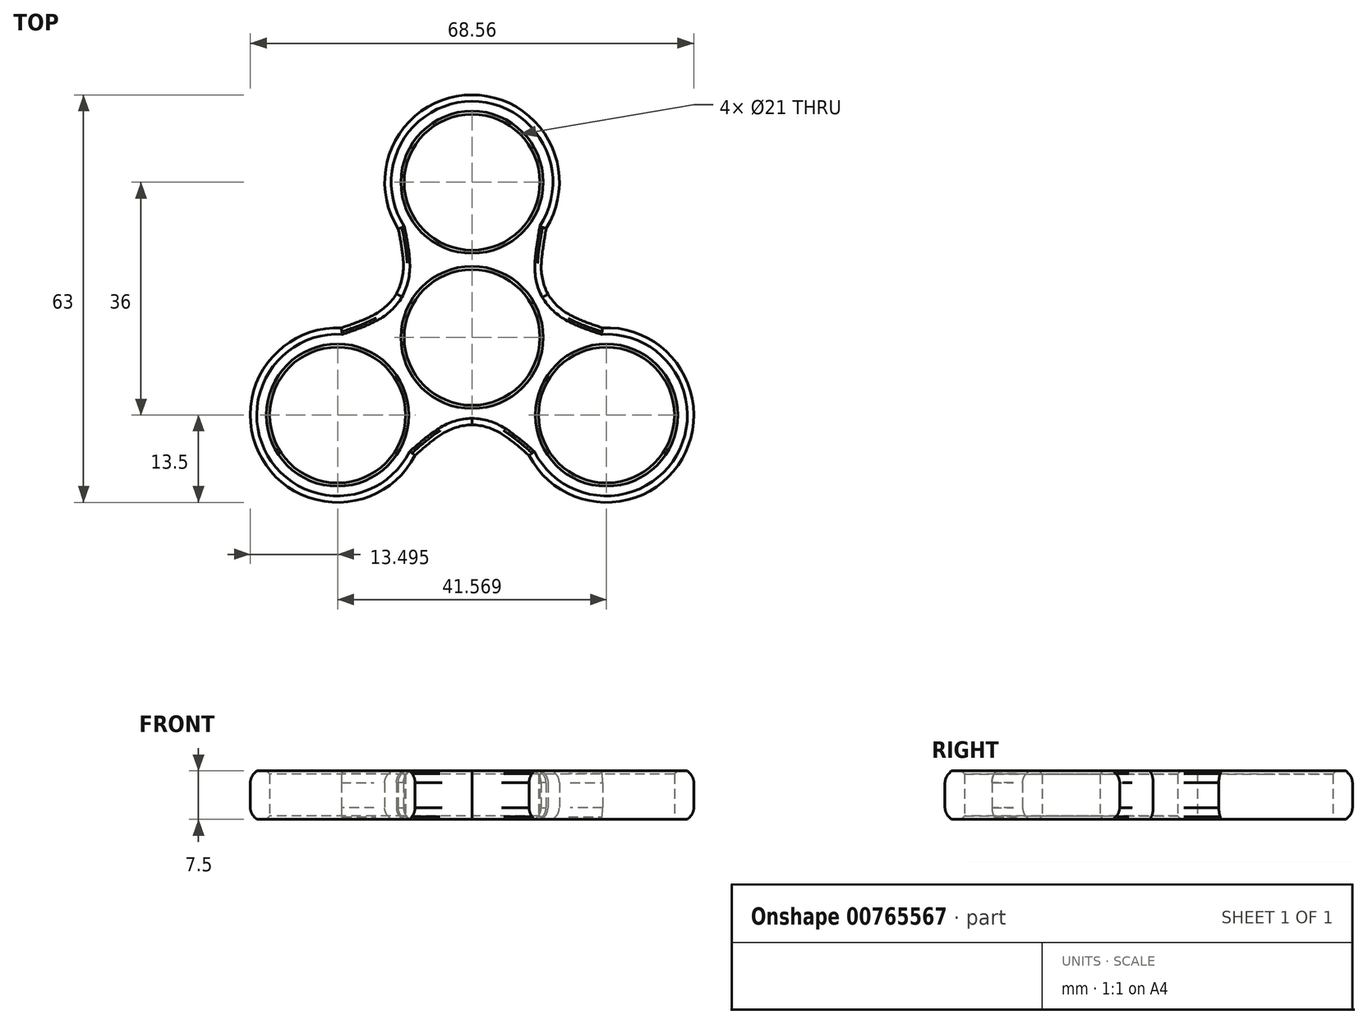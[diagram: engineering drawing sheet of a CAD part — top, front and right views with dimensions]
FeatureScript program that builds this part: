
annotation { "Feature Type Name" : "Feature", "Feature Type Description" : "" }
export const myFeature = defineFeature(function(context is Context, id is Id, definition is map)
    precondition{}
    {
        {
            var Q0;
            Q0=qCreatedBy(makeId("Top.planeOp"),FACE);
            var sketch = newSketch(context, id + "F0", { "sketchPlane" : qUnion([Q0])});
            skCircle(sketch, "E0", {"center": v(0, 0) * mm, "radius": 10.5 * mm});
            skSolve(sketch);
        }
        {
            var Q0;
            Q0=makeQuery(id+"F0.imprint","IMPRINT",FACE,{"disambiguationData":[TD([[makeQuery(id+"F0.imprint","IMPRINT",EDGE,{"derivedFrom":sQuery(id+"F0.wireOp",EDGE,"E0")}),1.0]])]});
            var sketch = newSketch(context, id + "F1", { "sketchPlane" : qUnion([Q0])});
            skCircle(sketch, "E1.0", {"center": v(0, 0) * mm, "radius": 13.5 * mm});
            skSolve(sketch);
        }
        {
            var Q0;
            Q0=qCreatedBy(makeId("Top.planeOp"),FACE);
            var sketch = newSketch(context, id + "F2", { "sketchPlane" : qUnion([Q0])});
            skCircle(sketch, "E2", {"center": v(0, 24) * mm, "radius": 10.5 * mm});
            skLineSegment(sketch, "E3", {"start": v(0, 0) * mm, "end": v(0, 24) * mm, "construction": true});
            skSolve(sketch);
        }
        {
            var Q0;
            Q0=qCreatedBy(makeId("Top.planeOp"),FACE);
            var sketch = newSketch(context, id + "F3", { "sketchPlane" : qUnion([Q0])});
            skLineSegment(sketch, "E4", {"start": v(0, 0) * mm, "end": v(20.78, -12) * mm, "construction": true});
            skPoint(sketch, "E5", {"position": v(20.78, -12) * mm});
            skCircle(sketch, "E6", {"center": v(20.78, -12) * mm, "radius": 10.5 * mm});
            skSolve(sketch);
        }
        {
            var Q0;
            Q0=qCreatedBy(makeId("Top.planeOp"),FACE);
            var sketch = newSketch(context, id + "F4", { "sketchPlane" : qUnion([Q0])});
            skLineSegment(sketch, "E7", {"start": v(0, 0) * mm, "end": v(-20.78, -12) * mm, "construction": true});
            skPoint(sketch, "E8", {"position": v(-20.78, -12) * mm});
            skCircle(sketch, "E9", {"center": v(-20.78, -12) * mm, "radius": 10.5 * mm});
            skSolve(sketch);
        }
        {
            var Q0;
            Q0=makeQuery(id+"F4.imprint","IMPRINT",FACE,{"disambiguationData":[TD([[makeQuery(id+"F4.imprint","IMPRINT",EDGE,{"derivedFrom":sQuery(id+"F4.wireOp",EDGE,"E9")}),1.0]])]});
            var sketch = newSketch(context, id + "F5", { "sketchPlane" : qUnion([Q0])});
            skCircle(sketch, "E10.0", {"center": v(-20.78, -12) * mm, "radius": 13.5 * mm});
            skCircle(sketch, "E11.0", {"center": v(20.78, -12) * mm, "radius": 13.5 * mm});
            skCircle(sketch, "E12.0", {"center": v(0, 24) * mm, "radius": 13.5 * mm});
            skSolve(sketch);
        }
        {
            var Q0;
            Q0=qCreatedBy(makeId("Top.planeOp"),FACE);
            var sketch = newSketch(context, id + "F6", { "sketchPlane" : qUnion([Q0])});
            skLineSegment(sketch, "E13", {"start": v(-20.78, -12) * mm, "end": v(-20.78, 1.3) * mm, "construction": true});
            skPoint(sketch, "E14", {"position": v(-20.78, 1.3) * mm});
            skSolve(sketch);
        }
        {
            var Q0;
            Q0=qCreatedBy(makeId("Top.planeOp"),FACE);
            var sketch = newSketch(context, id + "F7", { "sketchPlane" : qUnion([Q0])});
            skLineSegment(sketch, "E15", {"start": v(20.78, -12) * mm, "end": v(20.78, 1.3) * mm, "construction": true});
            skPoint(sketch, "E16", {"position": v(20.78, 1.3) * mm});
            skSolve(sketch);
        }
        {
            var Q0;
            Q0=qCreatedBy(makeId("Top.planeOp"),FACE);
            var sketch = newSketch(context, id + "F8", { "sketchPlane" : qUnion([Q0])});
            skLineSegment(sketch, "E17", {"start": v(20.78, -12) * mm, "end": v(9.27, -18.65) * mm, "construction": true});
            skPoint(sketch, "E18", {"position": v(9.27, -18.65) * mm});
            skSolve(sketch);
        }
        {
            var Q0;
            Q0=qCreatedBy(makeId("Top.planeOp"),FACE);
            var sketch = newSketch(context, id + "F9", { "sketchPlane" : qUnion([Q0])});
            skLineSegment(sketch, "E19", {"start": v(-20.78, -12) * mm, "end": v(-9.27, -18.65) * mm, "construction": true});
            skPoint(sketch, "E20", {"position": v(-9.27, -18.65) * mm});
            skSolve(sketch);
        }
        {
            var Q0;
            Q0=qCreatedBy(makeId("Top.planeOp"),FACE);
            var sketch = newSketch(context, id + "F10", { "sketchPlane" : qUnion([Q0])});
            skLineSegment(sketch, "E21", {"start": v(0, 24) * mm, "end": v(11.52, 17.35) * mm, "construction": true});
            skPoint(sketch, "E22", {"position": v(11.52, 17.35) * mm});
            skSolve(sketch);
        }
        {
            var Q0;
            Q0=qCreatedBy(makeId("Top.planeOp"),FACE);
            var sketch = newSketch(context, id + "F11", { "sketchPlane" : qUnion([Q0])});
            skLineSegment(sketch, "E23", {"start": v(0, 24) * mm, "end": v(-11.52, 17.35) * mm, "construction": true});
            skPoint(sketch, "E24", {"position": v(-11.52, 17.35) * mm});
            skSolve(sketch);
        }
        {
            var Q0;
            Q0=qCreatedBy(makeId("Top.planeOp"),FACE);
            var sketch = newSketch(context, id + "F12", { "sketchPlane" : qUnion([Q0])});
            skLineSegment(sketch, "E25", {"start": v(0, 0) * mm, "end": v(-11.52, 6.65) * mm, "construction": true});
            skPoint(sketch, "E26", {"position": v(-11.52, 6.65) * mm});
            skSolve(sketch);
        }
        {
            var Q0;
            Q0=qCreatedBy(makeId("Top.planeOp"),FACE);
            var sketch = newSketch(context, id + "F13", { "sketchPlane" : qUnion([Q0])});
            skLineSegment(sketch, "E27", {"start": v(0, 0) * mm, "end": v(11.52, 6.65) * mm, "construction": true});
            skPoint(sketch, "E28", {"position": v(11.52, 6.65) * mm});
            skSolve(sketch);
        }
        {
            var Q0;
            Q0=qCreatedBy(makeId("Top.planeOp"),FACE);
            var sketch = newSketch(context, id + "F14", { "sketchPlane" : qUnion([Q0])});
            skLineSegment(sketch, "E29", {"start": v(0, 0) * mm, "end": v(0, -13.3) * mm, "construction": true});
            skPoint(sketch, "E30", {"position": v(0, -13.3) * mm});
            skSolve(sketch);
        }
        {
            var Q0;
            Q0=qCreatedBy(makeId("Top.planeOp"),FACE);
            var sketch = newSketch(context, id + "F15", { "sketchPlane" : qUnion([Q0])});
            skFitSpline(sketch, "E31", {"points": [v(-20.78, 1.3) * mm, v(-11.52, 6.65) * mm, v(-11.52, 17.35) * mm], "startDerivative": vector(21.66, 7.06) * mm, "endDerivative": vector(-4.63, 23.05) * mm});
            skLineSegment(sketch, "E32", {"start": v(-20.78, 1.3) * mm, "end": v(-17.62, -0.3) * mm});
            skLineSegment(sketch, "E33", {"start": v(-17.62, -0.3) * mm, "end": v(-12.18, -1.05) * mm});
            skLineSegment(sketch, "E34", {"start": v(-12.18, -1.05) * mm, "end": v(-8.59, 9.21) * mm});
            skLineSegment(sketch, "E35", {"start": v(-8.59, 9.21) * mm, "end": v(-5.34, 11.64) * mm});
            skLineSegment(sketch, "E36", {"start": v(-5.34, 11.64) * mm, "end": v(-11.52, 17.35) * mm});
            skSolve(sketch);
        }
        {
            var Q0;
            Q0=qCreatedBy(makeId("Top.planeOp"),FACE);
            var sketch = newSketch(context, id + "F16", { "sketchPlane" : qUnion([Q0])});
            skFitSpline(sketch, "E37", {"points": [v(20.78, 1.3) * mm, v(11.52, 6.65) * mm, v(11.52, 17.35) * mm], "startDerivative": vector(-20.8, 6.31) * mm, "endDerivative": vector(3.23, 22.6) * mm});
            skLineSegment(sketch, "E38", {"start": v(11.52, 17.35) * mm, "end": v(5.33, 11.85) * mm});
            skLineSegment(sketch, "E39", {"start": v(5.33, 11.85) * mm, "end": v(13.1, -1.66) * mm});
            skLineSegment(sketch, "E40", {"start": v(13.1, -1.66) * mm, "end": v(20.78, 1.3) * mm});
            skSolve(sketch);
        }
        {
            var Q0;
            Q0=qCreatedBy(makeId("Top.planeOp"),FACE);
            var sketch = newSketch(context, id + "F17", { "sketchPlane" : qUnion([Q0])});
            skFitSpline(sketch, "E41", {"points": [v(-9.27, -18.65) * mm, v(0, -13.3) * mm, v(9.27, -18.65) * mm], "startDerivative": vector(16.43, 14.9) * mm, "endDerivative": vector(16.46, -14.71) * mm});
            skLineSegment(sketch, "E42", {"start": v(9.27, -18.65) * mm, "end": v(7.72, -10.63) * mm});
            skLineSegment(sketch, "E43", {"start": v(7.72, -10.63) * mm, "end": v(-7.8, -10.9) * mm});
            skLineSegment(sketch, "E44", {"start": v(-7.8, -10.9) * mm, "end": v(-9.27, -18.65) * mm});
            skSolve(sketch);
        }
        {
            var Q0;
            Q0=makeQuery(id+"F5.imprint","IMPRINT",FACE,{"disambiguationData":[TD([[makeQuery(id+"F5.imprint","IMPRINT",EDGE,{"derivedFrom":sQuery(id+"F5.wireOp",EDGE,"E11.0")}),1.0]])]});
            var Q1;
            Q1=makeQuery(id+"F5.imprint","IMPRINT",FACE,{"disambiguationData":[TD([[makeQuery(id+"F5.imprint","IMPRINT",EDGE,{"derivedFrom":sQuery(id+"F5.wireOp",EDGE,"E12.0")}),1.0]])]});
            var Q2;
            Q2=makeQuery(id+"F5.imprint","IMPRINT",FACE,{"disambiguationData":[TD([[makeQuery(id+"F5.imprint","IMPRINT",EDGE,{"derivedFrom":sQuery(id+"F5.wireOp",EDGE,"E10.0")}),1.0]])]});
            var Q3;
            Q3=makeQuery(id+"F1.imprint","IMPRINT",FACE,{"disambiguationData":[TD([[makeQuery(id+"F1.imprint","IMPRINT",EDGE,{"derivedFrom":sQuery(id+"F1.wireOp",EDGE,"E1.0")}),1.0]])]});
            var Q4;
            Q4=makeQuery(id+"F15.imprint","IMPRINT",FACE,{"disambiguationData":[TD([[makeQuery(id+"F15.imprint","IMPRINT",EDGE,{"derivedFrom":sQuery(id+"F15.wireOp",EDGE,"E31")}),-1.0]])]});
            var Q5;
            Q5=makeQuery(id+"F16.imprint","IMPRINT",FACE,{"disambiguationData":[TD([[makeQuery(id+"F16.imprint","IMPRINT",EDGE,{"derivedFrom":sQuery(id+"F16.wireOp",EDGE,"E37")}),1.0]])]});
            var Q6;
            Q6=makeQuery(id+"F17.imprint","IMPRINT",FACE,{"disambiguationData":[TD([[makeQuery(id+"F17.imprint","IMPRINT",EDGE,{"derivedFrom":sQuery(id+"F17.wireOp",EDGE,"E41")}),1.0]])]});
            extrude(context, id + "F18", {"entities" : qUnion([Q0, Q1, Q2, Q3, Q4, Q5, Q6]), "depth" : 7.5 * mm, "offsetDistance" : 25 * mm});
        }
        {
            var Q0;
            Q0=makeQuery(id+"F3.imprint","IMPRINT",FACE,{"disambiguationData":[TD([[makeQuery(id+"F3.imprint","IMPRINT",EDGE,{"derivedFrom":sQuery(id+"F3.wireOp",EDGE,"E6")}),1.0]])]});
            extrude(context, id + "F19", {"entities" : qUnion([Q0]), "operationType" : NewBodyOperationType.REMOVE, "depth" : 39.8 * mm, "offsetDistance" : 25 * mm});
        }
        {
            var Q0;
            Q0=makeQuery(id+"F2.imprint","IMPRINT",FACE,{"disambiguationData":[TD([[makeQuery(id+"F2.imprint","IMPRINT",EDGE,{"derivedFrom":sQuery(id+"F2.wireOp",EDGE,"E2")}),1.0]])]});
            extrude(context, id + "F20", {"entities" : qUnion([Q0]), "operationType" : NewBodyOperationType.REMOVE, "depth" : 25 * mm, "offsetDistance" : 25 * mm});
        }
        {
            var Q0;
            Q0=makeQuery(id+"F18.opExtrude","SWEPT_BODY",BODY,{"disambiguationData":[OSD([sQuery(id+"F4.wireOp",EDGE,"E9"),sQuery(id+"F5.wireOp",EDGE,"E10.0")])]});
            var Q1;
            Q1=makeQuery(id+"F18.opExtrude","SWEPT_BODY",BODY,{"disambiguationData":[OSD([sQuery(id+"F15.wireOp",EDGE,"E31"),sQuery(id+"F15.wireOp",EDGE,"E32"),sQuery(id+"F15.wireOp",EDGE,"E33"),sQuery(id+"F15.wireOp",EDGE,"E34"),sQuery(id+"F15.wireOp",EDGE,"E35"),sQuery(id+"F15.wireOp",EDGE,"E36")])]});
            var Q2;
            Q2=makeQuery(id+"F18.opExtrude","SWEPT_BODY",BODY,{"disambiguationData":[OSD([sQuery(id+"F0.wireOp",EDGE,"E0"),sQuery(id+"F1.wireOp",EDGE,"E1.0")])]});
            var Q3;
            Q3=makeQuery(id+"F18.opExtrude","SWEPT_BODY",BODY,{"disambiguationData":[OSD([sQuery(id+"F5.wireOp",EDGE,"E11.0")])]});
            var Q4;
            Q4=makeQuery(id+"F18.opExtrude","SWEPT_BODY",BODY,{"disambiguationData":[OSD([sQuery(id+"F17.wireOp",EDGE,"E41"),sQuery(id+"F17.wireOp",EDGE,"E42"),sQuery(id+"F17.wireOp",EDGE,"E43"),sQuery(id+"F17.wireOp",EDGE,"E44")])]});
            var Q5;
            Q5=makeQuery(id+"F18.opExtrude","SWEPT_BODY",BODY,{"disambiguationData":[OSD([sQuery(id+"F5.wireOp",EDGE,"E12.0")])]});
            var Q6;
            Q6=makeQuery(id+"F18.opExtrude","SWEPT_BODY",BODY,{"disambiguationData":[OSD([sQuery(id+"F16.wireOp",EDGE,"E37"),sQuery(id+"F16.wireOp",EDGE,"E38"),sQuery(id+"F16.wireOp",EDGE,"E39"),sQuery(id+"F16.wireOp",EDGE,"E40")])]});
            booleanBodies(context, id + "F21", {"operationType" : BooleanOperationType.UNION, "tools" : qUnion([Q0, Q1, Q2, Q3, Q4, Q5, Q6])});
        }
        {
            var Q0;
            Q0=makeQuery(id+"F21.opBoolean","INTERSECT",EDGE,{"disambiguationData":[OD(1.0)],"derivedFrom":[makeQuery(id+"F18.opExtrude","SWEPT_FACE",FACE,{"disambiguationData":[OSD([sQuery(id+"F1.wireOp",EDGE,"E1.0")])]}),makeQuery(id+"F18.opExtrude","SWEPT_FACE",FACE,{"disambiguationData":[OSD([sQuery(id+"F16.wireOp",EDGE,"E37")])]})]});
            var Q1;
            Q1=makeQuery(id+"F21.opBoolean","INTERSECT",EDGE,{"disambiguationData":[OD(0.0)],"derivedFrom":[makeQuery(id+"F18.opExtrude","SWEPT_FACE",FACE,{"disambiguationData":[OSD([sQuery(id+"F1.wireOp",EDGE,"E1.0")])]}),makeQuery(id+"F18.opExtrude","SWEPT_FACE",FACE,{"disambiguationData":[OSD([sQuery(id+"F16.wireOp",EDGE,"E37")])]})]});
            fillet(context, id + "F22", {"entities" : qUnion([Q0, Q1]), "radius" : 9 * mm, "tangentPropagation" : true, "allowEdgeOverflow" : false});
        }
        {
            var Q0;
            Q0=makeQuery(id+"F21.opBoolean","INTERSECT",EDGE,{"disambiguationData":[OD(0.0)],"derivedFrom":[makeQuery(id+"F18.opExtrude","SWEPT_FACE",FACE,{"disambiguationData":[OSD([sQuery(id+"F1.wireOp",EDGE,"E1.0")])]}),makeQuery(id+"F18.opExtrude","SWEPT_FACE",FACE,{"disambiguationData":[OSD([sQuery(id+"F17.wireOp",EDGE,"E41")])]})]});
            var Q1;
            Q1=makeQuery(id+"F21.opBoolean","INTERSECT",EDGE,{"disambiguationData":[OD(1.0)],"derivedFrom":[makeQuery(id+"F18.opExtrude","SWEPT_FACE",FACE,{"disambiguationData":[OSD([sQuery(id+"F1.wireOp",EDGE,"E1.0")])]}),makeQuery(id+"F18.opExtrude","SWEPT_FACE",FACE,{"disambiguationData":[OSD([sQuery(id+"F17.wireOp",EDGE,"E41")])]})]});
            fillet(context, id + "F23", {"entities" : qUnion([Q0, Q1]), "radius" : 9 * mm, "tangentPropagation" : true, "allowEdgeOverflow" : false});
        }
        {
            var Q0;
            Q0=makeQuery(id+"F21.opBoolean","INTERSECT",EDGE,{"disambiguationData":[OD(1.0)],"derivedFrom":[makeQuery(id+"F18.opExtrude","SWEPT_FACE",FACE,{"disambiguationData":[OSD([sQuery(id+"F1.wireOp",EDGE,"E1.0")])]}),makeQuery(id+"F18.opExtrude","SWEPT_FACE",FACE,{"disambiguationData":[OSD([sQuery(id+"F15.wireOp",EDGE,"E31")])]})]});
            var Q1;
            Q1=makeQuery(id+"F21.opBoolean","INTERSECT",EDGE,{"disambiguationData":[OD(0.0)],"derivedFrom":[makeQuery(id+"F18.opExtrude","SWEPT_FACE",FACE,{"disambiguationData":[OSD([sQuery(id+"F1.wireOp",EDGE,"E1.0")])]}),makeQuery(id+"F18.opExtrude","SWEPT_FACE",FACE,{"disambiguationData":[OSD([sQuery(id+"F15.wireOp",EDGE,"E31")])]})]});
            fillet(context, id + "F24", {"entities" : qUnion([Q0, Q1]), "radius" : 9 * mm, "tangentPropagation" : true, "allowEdgeOverflow" : false});
        }
        {
            var Q0;
            Q0=makeQuery(id+"F18.opExtrude","CAP_EDGE",EDGE,{"disambiguationData":[OSD([sQuery(id+"F0.wireOp",EDGE,"E0")])],"isStart":false});
            chamfer(context, id + "F25", {"entities" : qUnion([Q0]), "width" : 0.5 * mm, "tangentPropagation" : true});
        }
        {
            var Q0;
            Q0=makeQuery(id+"F19.boolean.opBoolean","INTERSECT",EDGE,{"derivedFrom":[makeQuery(id+"F18.opExtrude","CAP_FACE",FACE,{"disambiguationData":[OSD([sQuery(id+"F5.wireOp",EDGE,"E11.0")])],"isStart":false}),makeQuery(id+"F19.opExtrude","SWEPT_FACE",FACE,{"disambiguationData":[OSD([sQuery(id+"F3.wireOp",EDGE,"E6")])]})]});
            var Q1;
            Q1=makeQuery(id+"F18.opExtrude","CAP_EDGE",EDGE,{"disambiguationData":[OSD([sQuery(id+"F4.wireOp",EDGE,"E9")])],"isStart":false});
            var Q2;
            Q2=makeQuery(id+"F20.boolean.opBoolean","INTERSECT",EDGE,{"derivedFrom":[makeQuery(id+"F18.opExtrude","CAP_FACE",FACE,{"disambiguationData":[OSD([sQuery(id+"F5.wireOp",EDGE,"E12.0")])],"isStart":false}),makeQuery(id+"F20.opExtrude","SWEPT_FACE",FACE,{"disambiguationData":[OSD([sQuery(id+"F2.wireOp",EDGE,"E2")])]})]});
            chamfer(context, id + "F26", {"entities" : qUnion([Q0, Q1, Q2]), "width" : 0.5 * mm, "tangentPropagation" : true});
        }
        {
            var Q0;
            Q0=makeQuery(id+"F18.opExtrude","CAP_EDGE",EDGE,{"disambiguationData":[OSD([sQuery(id+"F5.wireOp",EDGE,"E11.0")])],"isStart":false});
            var Q1;
            {var subQ0=sQuery(id+"F5.wireOp",EDGE,"E11.0");var subQ2=sQuery(id+"F16.wireOp",EDGE,"E37");Q1=makeQuery(id+"F21.opBoolean","SPLIT",EDGE,{"disambiguationData":[TD([makeQuery(id+"F18.opExtrude","SWEPT_FACE",FACE,{"disambiguationData":[OSD([subQ0])]})])],"derivedFrom":makeQuery(id+"F18.opExtrude","CAP_EDGE",EDGE,{"disambiguationData":[OSD([subQ2])],"isStart":false})});}
            var Q2;
            {var subQ0=sQuery(id+"F16.wireOp",EDGE,"E37");var subQ1=sQuery(id+"F1.wireOp",EDGE,"E1.0");Q2=makeQuery(id+"F22.opFillet","BLEND_EDGE",EDGE,{"blendedFrom":[makeQuery(id+"F21.opBoolean","INTERSECT",EDGE,{"disambiguationData":[OD(0.0)],"derivedFrom":[makeQuery(id+"F18.opExtrude","SWEPT_FACE",FACE,{"disambiguationData":[OSD([subQ1])]}),makeQuery(id+"F18.opExtrude","SWEPT_FACE",FACE,{"disambiguationData":[OSD([subQ0])]})]}),makeQuery(id+"F21.opBoolean","MERGE",FACE,{"derivedFrom":[makeQuery(id+"F18.opExtrude","CAP_FACE",FACE,{"disambiguationData":[OSD([sQuery(id+"F0.wireOp",EDGE,"E0"),subQ1])],"isStart":false}),makeQuery(id+"F18.opExtrude","CAP_FACE",FACE,{"disambiguationData":[OSD([sQuery(id+"F4.wireOp",EDGE,"E9"),sQuery(id+"F5.wireOp",EDGE,"E10.0")])],"isStart":false}),makeQuery(id+"F18.opExtrude","CAP_FACE",FACE,{"disambiguationData":[OSD([sQuery(id+"F15.wireOp",EDGE,"E31"),sQuery(id+"F15.wireOp",EDGE,"E32"),sQuery(id+"F15.wireOp",EDGE,"E33"),sQuery(id+"F15.wireOp",EDGE,"E34"),sQuery(id+"F15.wireOp",EDGE,"E35"),sQuery(id+"F15.wireOp",EDGE,"E36")])],"isStart":false}),makeQuery(id+"F18.opExtrude","CAP_FACE",FACE,{"disambiguationData":[OSD([subQ0,sQuery(id+"F16.wireOp",EDGE,"E38"),sQuery(id+"F16.wireOp",EDGE,"E39"),sQuery(id+"F16.wireOp",EDGE,"E40")])],"isStart":false}),makeQuery(id+"F18.opExtrude","CAP_FACE",FACE,{"disambiguationData":[OSD([sQuery(id+"F17.wireOp",EDGE,"E41"),sQuery(id+"F17.wireOp",EDGE,"E42"),sQuery(id+"F17.wireOp",EDGE,"E43"),sQuery(id+"F17.wireOp",EDGE,"E44")])],"isStart":false}),makeQuery(id+"F18.opExtrude","CAP_FACE",FACE,{"disambiguationData":[OSD([sQuery(id+"F5.wireOp",EDGE,"E11.0")])],"isStart":false}),makeQuery(id+"F18.opExtrude","CAP_FACE",FACE,{"disambiguationData":[OSD([sQuery(id+"F5.wireOp",EDGE,"E12.0")])],"isStart":false})]})],"blendedInto":[makeQuery(id+"F21.opBoolean","MERGE",FACE,{"derivedFrom":[makeQuery(id+"F18.opExtrude","CAP_FACE",FACE,{"disambiguationData":[OSD([sQuery(id+"F0.wireOp",EDGE,"E0"),subQ1])],"isStart":false}),makeQuery(id+"F18.opExtrude","CAP_FACE",FACE,{"disambiguationData":[OSD([sQuery(id+"F4.wireOp",EDGE,"E9"),sQuery(id+"F5.wireOp",EDGE,"E10.0")])],"isStart":false}),makeQuery(id+"F18.opExtrude","CAP_FACE",FACE,{"disambiguationData":[OSD([sQuery(id+"F15.wireOp",EDGE,"E31"),sQuery(id+"F15.wireOp",EDGE,"E32"),sQuery(id+"F15.wireOp",EDGE,"E33"),sQuery(id+"F15.wireOp",EDGE,"E34"),sQuery(id+"F15.wireOp",EDGE,"E35"),sQuery(id+"F15.wireOp",EDGE,"E36")])],"isStart":false}),makeQuery(id+"F18.opExtrude","CAP_FACE",FACE,{"disambiguationData":[OSD([subQ0,sQuery(id+"F16.wireOp",EDGE,"E38"),sQuery(id+"F16.wireOp",EDGE,"E39"),sQuery(id+"F16.wireOp",EDGE,"E40")])],"isStart":false}),makeQuery(id+"F18.opExtrude","CAP_FACE",FACE,{"disambiguationData":[OSD([sQuery(id+"F17.wireOp",EDGE,"E41"),sQuery(id+"F17.wireOp",EDGE,"E42"),sQuery(id+"F17.wireOp",EDGE,"E43"),sQuery(id+"F17.wireOp",EDGE,"E44")])],"isStart":false}),makeQuery(id+"F18.opExtrude","CAP_FACE",FACE,{"disambiguationData":[OSD([sQuery(id+"F5.wireOp",EDGE,"E11.0")])],"isStart":false}),makeQuery(id+"F18.opExtrude","CAP_FACE",FACE,{"disambiguationData":[OSD([sQuery(id+"F5.wireOp",EDGE,"E12.0")])],"isStart":false})]})]});}
            var Q3;
            {var subQ0=sQuery(id+"F16.wireOp",EDGE,"E37");var subQ1=sQuery(id+"F1.wireOp",EDGE,"E1.0");Q3=makeQuery(id+"F22.opFillet","BLEND_EDGE",EDGE,{"blendedFrom":[makeQuery(id+"F21.opBoolean","INTERSECT",EDGE,{"disambiguationData":[OD(1.0)],"derivedFrom":[makeQuery(id+"F18.opExtrude","SWEPT_FACE",FACE,{"disambiguationData":[OSD([subQ1])]}),makeQuery(id+"F18.opExtrude","SWEPT_FACE",FACE,{"disambiguationData":[OSD([subQ0])]})]}),makeQuery(id+"F21.opBoolean","MERGE",FACE,{"derivedFrom":[makeQuery(id+"F18.opExtrude","CAP_FACE",FACE,{"disambiguationData":[OSD([sQuery(id+"F0.wireOp",EDGE,"E0"),subQ1])],"isStart":false}),makeQuery(id+"F18.opExtrude","CAP_FACE",FACE,{"disambiguationData":[OSD([sQuery(id+"F4.wireOp",EDGE,"E9"),sQuery(id+"F5.wireOp",EDGE,"E10.0")])],"isStart":false}),makeQuery(id+"F18.opExtrude","CAP_FACE",FACE,{"disambiguationData":[OSD([sQuery(id+"F15.wireOp",EDGE,"E31"),sQuery(id+"F15.wireOp",EDGE,"E32"),sQuery(id+"F15.wireOp",EDGE,"E33"),sQuery(id+"F15.wireOp",EDGE,"E34"),sQuery(id+"F15.wireOp",EDGE,"E35"),sQuery(id+"F15.wireOp",EDGE,"E36")])],"isStart":false}),makeQuery(id+"F18.opExtrude","CAP_FACE",FACE,{"disambiguationData":[OSD([subQ0,sQuery(id+"F16.wireOp",EDGE,"E38"),sQuery(id+"F16.wireOp",EDGE,"E39"),sQuery(id+"F16.wireOp",EDGE,"E40")])],"isStart":false}),makeQuery(id+"F18.opExtrude","CAP_FACE",FACE,{"disambiguationData":[OSD([sQuery(id+"F17.wireOp",EDGE,"E41"),sQuery(id+"F17.wireOp",EDGE,"E42"),sQuery(id+"F17.wireOp",EDGE,"E43"),sQuery(id+"F17.wireOp",EDGE,"E44")])],"isStart":false}),makeQuery(id+"F18.opExtrude","CAP_FACE",FACE,{"disambiguationData":[OSD([sQuery(id+"F5.wireOp",EDGE,"E11.0")])],"isStart":false}),makeQuery(id+"F18.opExtrude","CAP_FACE",FACE,{"disambiguationData":[OSD([sQuery(id+"F5.wireOp",EDGE,"E12.0")])],"isStart":false})]})],"blendedInto":[makeQuery(id+"F21.opBoolean","MERGE",FACE,{"derivedFrom":[makeQuery(id+"F18.opExtrude","CAP_FACE",FACE,{"disambiguationData":[OSD([sQuery(id+"F0.wireOp",EDGE,"E0"),subQ1])],"isStart":false}),makeQuery(id+"F18.opExtrude","CAP_FACE",FACE,{"disambiguationData":[OSD([sQuery(id+"F4.wireOp",EDGE,"E9"),sQuery(id+"F5.wireOp",EDGE,"E10.0")])],"isStart":false}),makeQuery(id+"F18.opExtrude","CAP_FACE",FACE,{"disambiguationData":[OSD([sQuery(id+"F15.wireOp",EDGE,"E31"),sQuery(id+"F15.wireOp",EDGE,"E32"),sQuery(id+"F15.wireOp",EDGE,"E33"),sQuery(id+"F15.wireOp",EDGE,"E34"),sQuery(id+"F15.wireOp",EDGE,"E35"),sQuery(id+"F15.wireOp",EDGE,"E36")])],"isStart":false}),makeQuery(id+"F18.opExtrude","CAP_FACE",FACE,{"disambiguationData":[OSD([subQ0,sQuery(id+"F16.wireOp",EDGE,"E38"),sQuery(id+"F16.wireOp",EDGE,"E39"),sQuery(id+"F16.wireOp",EDGE,"E40")])],"isStart":false}),makeQuery(id+"F18.opExtrude","CAP_FACE",FACE,{"disambiguationData":[OSD([sQuery(id+"F17.wireOp",EDGE,"E41"),sQuery(id+"F17.wireOp",EDGE,"E42"),sQuery(id+"F17.wireOp",EDGE,"E43"),sQuery(id+"F17.wireOp",EDGE,"E44")])],"isStart":false}),makeQuery(id+"F18.opExtrude","CAP_FACE",FACE,{"disambiguationData":[OSD([sQuery(id+"F5.wireOp",EDGE,"E11.0")])],"isStart":false}),makeQuery(id+"F18.opExtrude","CAP_FACE",FACE,{"disambiguationData":[OSD([sQuery(id+"F5.wireOp",EDGE,"E12.0")])],"isStart":false})]})]});}
            var Q4;
            {var subQ1=sQuery(id+"F16.wireOp",EDGE,"E37");var subQ2=sQuery(id+"F5.wireOp",EDGE,"E12.0");Q4=makeQuery(id+"F21.opBoolean","SPLIT",EDGE,{"disambiguationData":[TD([makeQuery(id+"F18.opExtrude","SWEPT_FACE",FACE,{"disambiguationData":[OSD([subQ2])]})])],"derivedFrom":makeQuery(id+"F18.opExtrude","CAP_EDGE",EDGE,{"disambiguationData":[OSD([subQ1])],"isStart":false})});}
            var Q5;
            Q5=makeQuery(id+"F18.opExtrude","CAP_EDGE",EDGE,{"disambiguationData":[OSD([sQuery(id+"F5.wireOp",EDGE,"E12.0")])],"isStart":false});
            var Q6;
            {var subQ1=sQuery(id+"F5.wireOp",EDGE,"E12.0");var subQ2=sQuery(id+"F15.wireOp",EDGE,"E31");Q6=makeQuery(id+"F21.opBoolean","SPLIT",EDGE,{"disambiguationData":[TD([makeQuery(id+"F18.opExtrude","SWEPT_FACE",FACE,{"disambiguationData":[OSD([subQ1])]})])],"derivedFrom":makeQuery(id+"F18.opExtrude","CAP_EDGE",EDGE,{"disambiguationData":[OSD([subQ2])],"isStart":false})});}
            var Q7;
            {var subQ0=sQuery(id+"F15.wireOp",EDGE,"E31");var subQ1=sQuery(id+"F1.wireOp",EDGE,"E1.0");Q7=makeQuery(id+"F24.opFillet","BLEND_EDGE",EDGE,{"blendedFrom":[makeQuery(id+"F21.opBoolean","INTERSECT",EDGE,{"disambiguationData":[OD(1.0)],"derivedFrom":[makeQuery(id+"F18.opExtrude","SWEPT_FACE",FACE,{"disambiguationData":[OSD([subQ1])]}),makeQuery(id+"F18.opExtrude","SWEPT_FACE",FACE,{"disambiguationData":[OSD([subQ0])]})]}),makeQuery(id+"F21.opBoolean","MERGE",FACE,{"derivedFrom":[makeQuery(id+"F18.opExtrude","CAP_FACE",FACE,{"disambiguationData":[OSD([sQuery(id+"F0.wireOp",EDGE,"E0"),subQ1])],"isStart":false}),makeQuery(id+"F18.opExtrude","CAP_FACE",FACE,{"disambiguationData":[OSD([sQuery(id+"F4.wireOp",EDGE,"E9"),sQuery(id+"F5.wireOp",EDGE,"E10.0")])],"isStart":false}),makeQuery(id+"F18.opExtrude","CAP_FACE",FACE,{"disambiguationData":[OSD([subQ0,sQuery(id+"F15.wireOp",EDGE,"E32"),sQuery(id+"F15.wireOp",EDGE,"E33"),sQuery(id+"F15.wireOp",EDGE,"E34"),sQuery(id+"F15.wireOp",EDGE,"E35"),sQuery(id+"F15.wireOp",EDGE,"E36")])],"isStart":false}),makeQuery(id+"F18.opExtrude","CAP_FACE",FACE,{"disambiguationData":[OSD([sQuery(id+"F16.wireOp",EDGE,"E37"),sQuery(id+"F16.wireOp",EDGE,"E38"),sQuery(id+"F16.wireOp",EDGE,"E39"),sQuery(id+"F16.wireOp",EDGE,"E40")])],"isStart":false}),makeQuery(id+"F18.opExtrude","CAP_FACE",FACE,{"disambiguationData":[OSD([sQuery(id+"F17.wireOp",EDGE,"E41"),sQuery(id+"F17.wireOp",EDGE,"E42"),sQuery(id+"F17.wireOp",EDGE,"E43"),sQuery(id+"F17.wireOp",EDGE,"E44")])],"isStart":false}),makeQuery(id+"F18.opExtrude","CAP_FACE",FACE,{"disambiguationData":[OSD([sQuery(id+"F5.wireOp",EDGE,"E11.0")])],"isStart":false}),makeQuery(id+"F18.opExtrude","CAP_FACE",FACE,{"disambiguationData":[OSD([sQuery(id+"F5.wireOp",EDGE,"E12.0")])],"isStart":false})]})],"blendedInto":[makeQuery(id+"F21.opBoolean","MERGE",FACE,{"derivedFrom":[makeQuery(id+"F18.opExtrude","CAP_FACE",FACE,{"disambiguationData":[OSD([sQuery(id+"F0.wireOp",EDGE,"E0"),subQ1])],"isStart":false}),makeQuery(id+"F18.opExtrude","CAP_FACE",FACE,{"disambiguationData":[OSD([sQuery(id+"F4.wireOp",EDGE,"E9"),sQuery(id+"F5.wireOp",EDGE,"E10.0")])],"isStart":false}),makeQuery(id+"F18.opExtrude","CAP_FACE",FACE,{"disambiguationData":[OSD([subQ0,sQuery(id+"F15.wireOp",EDGE,"E32"),sQuery(id+"F15.wireOp",EDGE,"E33"),sQuery(id+"F15.wireOp",EDGE,"E34"),sQuery(id+"F15.wireOp",EDGE,"E35"),sQuery(id+"F15.wireOp",EDGE,"E36")])],"isStart":false}),makeQuery(id+"F18.opExtrude","CAP_FACE",FACE,{"disambiguationData":[OSD([sQuery(id+"F16.wireOp",EDGE,"E37"),sQuery(id+"F16.wireOp",EDGE,"E38"),sQuery(id+"F16.wireOp",EDGE,"E39"),sQuery(id+"F16.wireOp",EDGE,"E40")])],"isStart":false}),makeQuery(id+"F18.opExtrude","CAP_FACE",FACE,{"disambiguationData":[OSD([sQuery(id+"F17.wireOp",EDGE,"E41"),sQuery(id+"F17.wireOp",EDGE,"E42"),sQuery(id+"F17.wireOp",EDGE,"E43"),sQuery(id+"F17.wireOp",EDGE,"E44")])],"isStart":false}),makeQuery(id+"F18.opExtrude","CAP_FACE",FACE,{"disambiguationData":[OSD([sQuery(id+"F5.wireOp",EDGE,"E11.0")])],"isStart":false}),makeQuery(id+"F18.opExtrude","CAP_FACE",FACE,{"disambiguationData":[OSD([sQuery(id+"F5.wireOp",EDGE,"E12.0")])],"isStart":false})]})]});}
            var Q8;
            {var subQ0=sQuery(id+"F15.wireOp",EDGE,"E31");var subQ1=sQuery(id+"F1.wireOp",EDGE,"E1.0");Q8=makeQuery(id+"F24.opFillet","BLEND_EDGE",EDGE,{"blendedFrom":[makeQuery(id+"F21.opBoolean","INTERSECT",EDGE,{"disambiguationData":[OD(0.0)],"derivedFrom":[makeQuery(id+"F18.opExtrude","SWEPT_FACE",FACE,{"disambiguationData":[OSD([subQ1])]}),makeQuery(id+"F18.opExtrude","SWEPT_FACE",FACE,{"disambiguationData":[OSD([subQ0])]})]}),makeQuery(id+"F21.opBoolean","MERGE",FACE,{"derivedFrom":[makeQuery(id+"F18.opExtrude","CAP_FACE",FACE,{"disambiguationData":[OSD([sQuery(id+"F0.wireOp",EDGE,"E0"),subQ1])],"isStart":false}),makeQuery(id+"F18.opExtrude","CAP_FACE",FACE,{"disambiguationData":[OSD([sQuery(id+"F4.wireOp",EDGE,"E9"),sQuery(id+"F5.wireOp",EDGE,"E10.0")])],"isStart":false}),makeQuery(id+"F18.opExtrude","CAP_FACE",FACE,{"disambiguationData":[OSD([subQ0,sQuery(id+"F15.wireOp",EDGE,"E32"),sQuery(id+"F15.wireOp",EDGE,"E33"),sQuery(id+"F15.wireOp",EDGE,"E34"),sQuery(id+"F15.wireOp",EDGE,"E35"),sQuery(id+"F15.wireOp",EDGE,"E36")])],"isStart":false}),makeQuery(id+"F18.opExtrude","CAP_FACE",FACE,{"disambiguationData":[OSD([sQuery(id+"F16.wireOp",EDGE,"E37"),sQuery(id+"F16.wireOp",EDGE,"E38"),sQuery(id+"F16.wireOp",EDGE,"E39"),sQuery(id+"F16.wireOp",EDGE,"E40")])],"isStart":false}),makeQuery(id+"F18.opExtrude","CAP_FACE",FACE,{"disambiguationData":[OSD([sQuery(id+"F17.wireOp",EDGE,"E41"),sQuery(id+"F17.wireOp",EDGE,"E42"),sQuery(id+"F17.wireOp",EDGE,"E43"),sQuery(id+"F17.wireOp",EDGE,"E44")])],"isStart":false}),makeQuery(id+"F18.opExtrude","CAP_FACE",FACE,{"disambiguationData":[OSD([sQuery(id+"F5.wireOp",EDGE,"E11.0")])],"isStart":false}),makeQuery(id+"F18.opExtrude","CAP_FACE",FACE,{"disambiguationData":[OSD([sQuery(id+"F5.wireOp",EDGE,"E12.0")])],"isStart":false})]})],"blendedInto":[makeQuery(id+"F21.opBoolean","MERGE",FACE,{"derivedFrom":[makeQuery(id+"F18.opExtrude","CAP_FACE",FACE,{"disambiguationData":[OSD([sQuery(id+"F0.wireOp",EDGE,"E0"),subQ1])],"isStart":false}),makeQuery(id+"F18.opExtrude","CAP_FACE",FACE,{"disambiguationData":[OSD([sQuery(id+"F4.wireOp",EDGE,"E9"),sQuery(id+"F5.wireOp",EDGE,"E10.0")])],"isStart":false}),makeQuery(id+"F18.opExtrude","CAP_FACE",FACE,{"disambiguationData":[OSD([subQ0,sQuery(id+"F15.wireOp",EDGE,"E32"),sQuery(id+"F15.wireOp",EDGE,"E33"),sQuery(id+"F15.wireOp",EDGE,"E34"),sQuery(id+"F15.wireOp",EDGE,"E35"),sQuery(id+"F15.wireOp",EDGE,"E36")])],"isStart":false}),makeQuery(id+"F18.opExtrude","CAP_FACE",FACE,{"disambiguationData":[OSD([sQuery(id+"F16.wireOp",EDGE,"E37"),sQuery(id+"F16.wireOp",EDGE,"E38"),sQuery(id+"F16.wireOp",EDGE,"E39"),sQuery(id+"F16.wireOp",EDGE,"E40")])],"isStart":false}),makeQuery(id+"F18.opExtrude","CAP_FACE",FACE,{"disambiguationData":[OSD([sQuery(id+"F17.wireOp",EDGE,"E41"),sQuery(id+"F17.wireOp",EDGE,"E42"),sQuery(id+"F17.wireOp",EDGE,"E43"),sQuery(id+"F17.wireOp",EDGE,"E44")])],"isStart":false}),makeQuery(id+"F18.opExtrude","CAP_FACE",FACE,{"disambiguationData":[OSD([sQuery(id+"F5.wireOp",EDGE,"E11.0")])],"isStart":false}),makeQuery(id+"F18.opExtrude","CAP_FACE",FACE,{"disambiguationData":[OSD([sQuery(id+"F5.wireOp",EDGE,"E12.0")])],"isStart":false})]})]});}
            var Q9;
            {var subQ0=sQuery(id+"F5.wireOp",EDGE,"E10.0");var subQ2=sQuery(id+"F15.wireOp",EDGE,"E31");Q9=makeQuery(id+"F21.opBoolean","SPLIT",EDGE,{"disambiguationData":[TD([makeQuery(id+"F18.opExtrude","SWEPT_FACE",FACE,{"disambiguationData":[OSD([subQ0])]})])],"derivedFrom":makeQuery(id+"F18.opExtrude","CAP_EDGE",EDGE,{"disambiguationData":[OSD([subQ2])],"isStart":false})});}
            var Q10;
            Q10=makeQuery(id+"F18.opExtrude","CAP_EDGE",EDGE,{"disambiguationData":[OSD([sQuery(id+"F5.wireOp",EDGE,"E10.0")])],"isStart":false});
            var Q11;
            {var subQ0=sQuery(id+"F5.wireOp",EDGE,"E10.0");var subQ1=sQuery(id+"F17.wireOp",EDGE,"E41");Q11=makeQuery(id+"F21.opBoolean","SPLIT",EDGE,{"disambiguationData":[TD([makeQuery(id+"F18.opExtrude","SWEPT_FACE",FACE,{"disambiguationData":[OSD([subQ0])]})])],"derivedFrom":makeQuery(id+"F18.opExtrude","CAP_EDGE",EDGE,{"disambiguationData":[OSD([subQ1])],"isStart":false})});}
            var Q12;
            {var subQ0=sQuery(id+"F17.wireOp",EDGE,"E41");var subQ1=sQuery(id+"F1.wireOp",EDGE,"E1.0");Q12=makeQuery(id+"F23.opFillet","BLEND_EDGE",EDGE,{"blendedFrom":[makeQuery(id+"F21.opBoolean","INTERSECT",EDGE,{"disambiguationData":[OD(0.0)],"derivedFrom":[makeQuery(id+"F18.opExtrude","SWEPT_FACE",FACE,{"disambiguationData":[OSD([subQ1])]}),makeQuery(id+"F18.opExtrude","SWEPT_FACE",FACE,{"disambiguationData":[OSD([subQ0])]})]}),makeQuery(id+"F21.opBoolean","MERGE",FACE,{"derivedFrom":[makeQuery(id+"F18.opExtrude","CAP_FACE",FACE,{"disambiguationData":[OSD([sQuery(id+"F0.wireOp",EDGE,"E0"),subQ1])],"isStart":false}),makeQuery(id+"F18.opExtrude","CAP_FACE",FACE,{"disambiguationData":[OSD([sQuery(id+"F4.wireOp",EDGE,"E9"),sQuery(id+"F5.wireOp",EDGE,"E10.0")])],"isStart":false}),makeQuery(id+"F18.opExtrude","CAP_FACE",FACE,{"disambiguationData":[OSD([sQuery(id+"F15.wireOp",EDGE,"E31"),sQuery(id+"F15.wireOp",EDGE,"E32"),sQuery(id+"F15.wireOp",EDGE,"E33"),sQuery(id+"F15.wireOp",EDGE,"E34"),sQuery(id+"F15.wireOp",EDGE,"E35"),sQuery(id+"F15.wireOp",EDGE,"E36")])],"isStart":false}),makeQuery(id+"F18.opExtrude","CAP_FACE",FACE,{"disambiguationData":[OSD([sQuery(id+"F16.wireOp",EDGE,"E37"),sQuery(id+"F16.wireOp",EDGE,"E38"),sQuery(id+"F16.wireOp",EDGE,"E39"),sQuery(id+"F16.wireOp",EDGE,"E40")])],"isStart":false}),makeQuery(id+"F18.opExtrude","CAP_FACE",FACE,{"disambiguationData":[OSD([subQ0,sQuery(id+"F17.wireOp",EDGE,"E42"),sQuery(id+"F17.wireOp",EDGE,"E43"),sQuery(id+"F17.wireOp",EDGE,"E44")])],"isStart":false}),makeQuery(id+"F18.opExtrude","CAP_FACE",FACE,{"disambiguationData":[OSD([sQuery(id+"F5.wireOp",EDGE,"E11.0")])],"isStart":false}),makeQuery(id+"F18.opExtrude","CAP_FACE",FACE,{"disambiguationData":[OSD([sQuery(id+"F5.wireOp",EDGE,"E12.0")])],"isStart":false})]})],"blendedInto":[makeQuery(id+"F21.opBoolean","MERGE",FACE,{"derivedFrom":[makeQuery(id+"F18.opExtrude","CAP_FACE",FACE,{"disambiguationData":[OSD([sQuery(id+"F0.wireOp",EDGE,"E0"),subQ1])],"isStart":false}),makeQuery(id+"F18.opExtrude","CAP_FACE",FACE,{"disambiguationData":[OSD([sQuery(id+"F4.wireOp",EDGE,"E9"),sQuery(id+"F5.wireOp",EDGE,"E10.0")])],"isStart":false}),makeQuery(id+"F18.opExtrude","CAP_FACE",FACE,{"disambiguationData":[OSD([sQuery(id+"F15.wireOp",EDGE,"E31"),sQuery(id+"F15.wireOp",EDGE,"E32"),sQuery(id+"F15.wireOp",EDGE,"E33"),sQuery(id+"F15.wireOp",EDGE,"E34"),sQuery(id+"F15.wireOp",EDGE,"E35"),sQuery(id+"F15.wireOp",EDGE,"E36")])],"isStart":false}),makeQuery(id+"F18.opExtrude","CAP_FACE",FACE,{"disambiguationData":[OSD([sQuery(id+"F16.wireOp",EDGE,"E37"),sQuery(id+"F16.wireOp",EDGE,"E38"),sQuery(id+"F16.wireOp",EDGE,"E39"),sQuery(id+"F16.wireOp",EDGE,"E40")])],"isStart":false}),makeQuery(id+"F18.opExtrude","CAP_FACE",FACE,{"disambiguationData":[OSD([subQ0,sQuery(id+"F17.wireOp",EDGE,"E42"),sQuery(id+"F17.wireOp",EDGE,"E43"),sQuery(id+"F17.wireOp",EDGE,"E44")])],"isStart":false}),makeQuery(id+"F18.opExtrude","CAP_FACE",FACE,{"disambiguationData":[OSD([sQuery(id+"F5.wireOp",EDGE,"E11.0")])],"isStart":false}),makeQuery(id+"F18.opExtrude","CAP_FACE",FACE,{"disambiguationData":[OSD([sQuery(id+"F5.wireOp",EDGE,"E12.0")])],"isStart":false})]})]});}
            var Q13;
            {var subQ0=sQuery(id+"F17.wireOp",EDGE,"E41");var subQ1=sQuery(id+"F1.wireOp",EDGE,"E1.0");Q13=makeQuery(id+"F23.opFillet","BLEND_EDGE",EDGE,{"blendedFrom":[makeQuery(id+"F21.opBoolean","INTERSECT",EDGE,{"disambiguationData":[OD(1.0)],"derivedFrom":[makeQuery(id+"F18.opExtrude","SWEPT_FACE",FACE,{"disambiguationData":[OSD([subQ1])]}),makeQuery(id+"F18.opExtrude","SWEPT_FACE",FACE,{"disambiguationData":[OSD([subQ0])]})]}),makeQuery(id+"F21.opBoolean","MERGE",FACE,{"derivedFrom":[makeQuery(id+"F18.opExtrude","CAP_FACE",FACE,{"disambiguationData":[OSD([sQuery(id+"F0.wireOp",EDGE,"E0"),subQ1])],"isStart":false}),makeQuery(id+"F18.opExtrude","CAP_FACE",FACE,{"disambiguationData":[OSD([sQuery(id+"F4.wireOp",EDGE,"E9"),sQuery(id+"F5.wireOp",EDGE,"E10.0")])],"isStart":false}),makeQuery(id+"F18.opExtrude","CAP_FACE",FACE,{"disambiguationData":[OSD([sQuery(id+"F15.wireOp",EDGE,"E31"),sQuery(id+"F15.wireOp",EDGE,"E32"),sQuery(id+"F15.wireOp",EDGE,"E33"),sQuery(id+"F15.wireOp",EDGE,"E34"),sQuery(id+"F15.wireOp",EDGE,"E35"),sQuery(id+"F15.wireOp",EDGE,"E36")])],"isStart":false}),makeQuery(id+"F18.opExtrude","CAP_FACE",FACE,{"disambiguationData":[OSD([sQuery(id+"F16.wireOp",EDGE,"E37"),sQuery(id+"F16.wireOp",EDGE,"E38"),sQuery(id+"F16.wireOp",EDGE,"E39"),sQuery(id+"F16.wireOp",EDGE,"E40")])],"isStart":false}),makeQuery(id+"F18.opExtrude","CAP_FACE",FACE,{"disambiguationData":[OSD([subQ0,sQuery(id+"F17.wireOp",EDGE,"E42"),sQuery(id+"F17.wireOp",EDGE,"E43"),sQuery(id+"F17.wireOp",EDGE,"E44")])],"isStart":false}),makeQuery(id+"F18.opExtrude","CAP_FACE",FACE,{"disambiguationData":[OSD([sQuery(id+"F5.wireOp",EDGE,"E11.0")])],"isStart":false}),makeQuery(id+"F18.opExtrude","CAP_FACE",FACE,{"disambiguationData":[OSD([sQuery(id+"F5.wireOp",EDGE,"E12.0")])],"isStart":false})]})],"blendedInto":[makeQuery(id+"F21.opBoolean","MERGE",FACE,{"derivedFrom":[makeQuery(id+"F18.opExtrude","CAP_FACE",FACE,{"disambiguationData":[OSD([sQuery(id+"F0.wireOp",EDGE,"E0"),subQ1])],"isStart":false}),makeQuery(id+"F18.opExtrude","CAP_FACE",FACE,{"disambiguationData":[OSD([sQuery(id+"F4.wireOp",EDGE,"E9"),sQuery(id+"F5.wireOp",EDGE,"E10.0")])],"isStart":false}),makeQuery(id+"F18.opExtrude","CAP_FACE",FACE,{"disambiguationData":[OSD([sQuery(id+"F15.wireOp",EDGE,"E31"),sQuery(id+"F15.wireOp",EDGE,"E32"),sQuery(id+"F15.wireOp",EDGE,"E33"),sQuery(id+"F15.wireOp",EDGE,"E34"),sQuery(id+"F15.wireOp",EDGE,"E35"),sQuery(id+"F15.wireOp",EDGE,"E36")])],"isStart":false}),makeQuery(id+"F18.opExtrude","CAP_FACE",FACE,{"disambiguationData":[OSD([sQuery(id+"F16.wireOp",EDGE,"E37"),sQuery(id+"F16.wireOp",EDGE,"E38"),sQuery(id+"F16.wireOp",EDGE,"E39"),sQuery(id+"F16.wireOp",EDGE,"E40")])],"isStart":false}),makeQuery(id+"F18.opExtrude","CAP_FACE",FACE,{"disambiguationData":[OSD([subQ0,sQuery(id+"F17.wireOp",EDGE,"E42"),sQuery(id+"F17.wireOp",EDGE,"E43"),sQuery(id+"F17.wireOp",EDGE,"E44")])],"isStart":false}),makeQuery(id+"F18.opExtrude","CAP_FACE",FACE,{"disambiguationData":[OSD([sQuery(id+"F5.wireOp",EDGE,"E11.0")])],"isStart":false}),makeQuery(id+"F18.opExtrude","CAP_FACE",FACE,{"disambiguationData":[OSD([sQuery(id+"F5.wireOp",EDGE,"E12.0")])],"isStart":false})]})]});}
            var Q14;
            {var subQ0=sQuery(id+"F17.wireOp",EDGE,"E41");var subQ1=sQuery(id+"F5.wireOp",EDGE,"E11.0");Q14=makeQuery(id+"F21.opBoolean","SPLIT",EDGE,{"disambiguationData":[TD([makeQuery(id+"F18.opExtrude","SWEPT_FACE",FACE,{"disambiguationData":[OSD([subQ1])]})])],"derivedFrom":makeQuery(id+"F18.opExtrude","CAP_EDGE",EDGE,{"disambiguationData":[OSD([subQ0])],"isStart":false})});}
            chamfer(context, id + "F27", {"entities" : qUnion([Q0, Q1, Q2, Q3, Q4, Q5, Q6, Q7, Q8, Q9, Q10, Q11, Q12, Q13, Q14]), "width" : 1 * mm, "tangentPropagation" : true});
        }
        {
            var Q0;
            Q0=makeQuery(id+"F18.opExtrude","CAP_EDGE",EDGE,{"disambiguationData":[OSD([sQuery(id+"F5.wireOp",EDGE,"E11.0")])],"isStart":true});
            var Q1;
            {var subQ0=sQuery(id+"F5.wireOp",EDGE,"E11.0");var subQ2=sQuery(id+"F16.wireOp",EDGE,"E37");Q1=makeQuery(id+"F21.opBoolean","SPLIT",EDGE,{"disambiguationData":[TD([makeQuery(id+"F18.opExtrude","SWEPT_FACE",FACE,{"disambiguationData":[OSD([subQ0])]})])],"derivedFrom":makeQuery(id+"F18.opExtrude","CAP_EDGE",EDGE,{"disambiguationData":[OSD([subQ2])],"isStart":true})});}
            var Q2;
            {var subQ0=sQuery(id+"F16.wireOp",EDGE,"E37");var subQ1=sQuery(id+"F1.wireOp",EDGE,"E1.0");Q2=makeQuery(id+"F22.opFillet","BLEND_EDGE",EDGE,{"blendedFrom":[makeQuery(id+"F21.opBoolean","INTERSECT",EDGE,{"disambiguationData":[OD(0.0)],"derivedFrom":[makeQuery(id+"F18.opExtrude","SWEPT_FACE",FACE,{"disambiguationData":[OSD([subQ1])]}),makeQuery(id+"F18.opExtrude","SWEPT_FACE",FACE,{"disambiguationData":[OSD([subQ0])]})]}),makeQuery(id+"F21.opBoolean","MERGE",FACE,{"derivedFrom":[makeQuery(id+"F18.opExtrude","CAP_FACE",FACE,{"disambiguationData":[OSD([sQuery(id+"F0.wireOp",EDGE,"E0"),subQ1])],"isStart":true}),makeQuery(id+"F18.opExtrude","CAP_FACE",FACE,{"disambiguationData":[OSD([sQuery(id+"F4.wireOp",EDGE,"E9"),sQuery(id+"F5.wireOp",EDGE,"E10.0")])],"isStart":true}),makeQuery(id+"F18.opExtrude","CAP_FACE",FACE,{"disambiguationData":[OSD([sQuery(id+"F15.wireOp",EDGE,"E31"),sQuery(id+"F15.wireOp",EDGE,"E32"),sQuery(id+"F15.wireOp",EDGE,"E33"),sQuery(id+"F15.wireOp",EDGE,"E34"),sQuery(id+"F15.wireOp",EDGE,"E35"),sQuery(id+"F15.wireOp",EDGE,"E36")])],"isStart":true}),makeQuery(id+"F18.opExtrude","CAP_FACE",FACE,{"disambiguationData":[OSD([subQ0,sQuery(id+"F16.wireOp",EDGE,"E38"),sQuery(id+"F16.wireOp",EDGE,"E39"),sQuery(id+"F16.wireOp",EDGE,"E40")])],"isStart":true}),makeQuery(id+"F18.opExtrude","CAP_FACE",FACE,{"disambiguationData":[OSD([sQuery(id+"F17.wireOp",EDGE,"E41"),sQuery(id+"F17.wireOp",EDGE,"E42"),sQuery(id+"F17.wireOp",EDGE,"E43"),sQuery(id+"F17.wireOp",EDGE,"E44")])],"isStart":true}),makeQuery(id+"F18.opExtrude","CAP_FACE",FACE,{"disambiguationData":[OSD([sQuery(id+"F5.wireOp",EDGE,"E11.0")])],"isStart":true}),makeQuery(id+"F18.opExtrude","CAP_FACE",FACE,{"disambiguationData":[OSD([sQuery(id+"F5.wireOp",EDGE,"E12.0")])],"isStart":true})]})],"blendedInto":[makeQuery(id+"F21.opBoolean","MERGE",FACE,{"derivedFrom":[makeQuery(id+"F18.opExtrude","CAP_FACE",FACE,{"disambiguationData":[OSD([sQuery(id+"F0.wireOp",EDGE,"E0"),subQ1])],"isStart":true}),makeQuery(id+"F18.opExtrude","CAP_FACE",FACE,{"disambiguationData":[OSD([sQuery(id+"F4.wireOp",EDGE,"E9"),sQuery(id+"F5.wireOp",EDGE,"E10.0")])],"isStart":true}),makeQuery(id+"F18.opExtrude","CAP_FACE",FACE,{"disambiguationData":[OSD([sQuery(id+"F15.wireOp",EDGE,"E31"),sQuery(id+"F15.wireOp",EDGE,"E32"),sQuery(id+"F15.wireOp",EDGE,"E33"),sQuery(id+"F15.wireOp",EDGE,"E34"),sQuery(id+"F15.wireOp",EDGE,"E35"),sQuery(id+"F15.wireOp",EDGE,"E36")])],"isStart":true}),makeQuery(id+"F18.opExtrude","CAP_FACE",FACE,{"disambiguationData":[OSD([subQ0,sQuery(id+"F16.wireOp",EDGE,"E38"),sQuery(id+"F16.wireOp",EDGE,"E39"),sQuery(id+"F16.wireOp",EDGE,"E40")])],"isStart":true}),makeQuery(id+"F18.opExtrude","CAP_FACE",FACE,{"disambiguationData":[OSD([sQuery(id+"F17.wireOp",EDGE,"E41"),sQuery(id+"F17.wireOp",EDGE,"E42"),sQuery(id+"F17.wireOp",EDGE,"E43"),sQuery(id+"F17.wireOp",EDGE,"E44")])],"isStart":true}),makeQuery(id+"F18.opExtrude","CAP_FACE",FACE,{"disambiguationData":[OSD([sQuery(id+"F5.wireOp",EDGE,"E11.0")])],"isStart":true}),makeQuery(id+"F18.opExtrude","CAP_FACE",FACE,{"disambiguationData":[OSD([sQuery(id+"F5.wireOp",EDGE,"E12.0")])],"isStart":true})]})]});}
            var Q3;
            {var subQ0=sQuery(id+"F16.wireOp",EDGE,"E37");var subQ1=sQuery(id+"F1.wireOp",EDGE,"E1.0");Q3=makeQuery(id+"F22.opFillet","BLEND_EDGE",EDGE,{"blendedFrom":[makeQuery(id+"F21.opBoolean","INTERSECT",EDGE,{"disambiguationData":[OD(1.0)],"derivedFrom":[makeQuery(id+"F18.opExtrude","SWEPT_FACE",FACE,{"disambiguationData":[OSD([subQ1])]}),makeQuery(id+"F18.opExtrude","SWEPT_FACE",FACE,{"disambiguationData":[OSD([subQ0])]})]}),makeQuery(id+"F21.opBoolean","MERGE",FACE,{"derivedFrom":[makeQuery(id+"F18.opExtrude","CAP_FACE",FACE,{"disambiguationData":[OSD([sQuery(id+"F0.wireOp",EDGE,"E0"),subQ1])],"isStart":true}),makeQuery(id+"F18.opExtrude","CAP_FACE",FACE,{"disambiguationData":[OSD([sQuery(id+"F4.wireOp",EDGE,"E9"),sQuery(id+"F5.wireOp",EDGE,"E10.0")])],"isStart":true}),makeQuery(id+"F18.opExtrude","CAP_FACE",FACE,{"disambiguationData":[OSD([sQuery(id+"F15.wireOp",EDGE,"E31"),sQuery(id+"F15.wireOp",EDGE,"E32"),sQuery(id+"F15.wireOp",EDGE,"E33"),sQuery(id+"F15.wireOp",EDGE,"E34"),sQuery(id+"F15.wireOp",EDGE,"E35"),sQuery(id+"F15.wireOp",EDGE,"E36")])],"isStart":true}),makeQuery(id+"F18.opExtrude","CAP_FACE",FACE,{"disambiguationData":[OSD([subQ0,sQuery(id+"F16.wireOp",EDGE,"E38"),sQuery(id+"F16.wireOp",EDGE,"E39"),sQuery(id+"F16.wireOp",EDGE,"E40")])],"isStart":true}),makeQuery(id+"F18.opExtrude","CAP_FACE",FACE,{"disambiguationData":[OSD([sQuery(id+"F17.wireOp",EDGE,"E41"),sQuery(id+"F17.wireOp",EDGE,"E42"),sQuery(id+"F17.wireOp",EDGE,"E43"),sQuery(id+"F17.wireOp",EDGE,"E44")])],"isStart":true}),makeQuery(id+"F18.opExtrude","CAP_FACE",FACE,{"disambiguationData":[OSD([sQuery(id+"F5.wireOp",EDGE,"E11.0")])],"isStart":true}),makeQuery(id+"F18.opExtrude","CAP_FACE",FACE,{"disambiguationData":[OSD([sQuery(id+"F5.wireOp",EDGE,"E12.0")])],"isStart":true})]})],"blendedInto":[makeQuery(id+"F21.opBoolean","MERGE",FACE,{"derivedFrom":[makeQuery(id+"F18.opExtrude","CAP_FACE",FACE,{"disambiguationData":[OSD([sQuery(id+"F0.wireOp",EDGE,"E0"),subQ1])],"isStart":true}),makeQuery(id+"F18.opExtrude","CAP_FACE",FACE,{"disambiguationData":[OSD([sQuery(id+"F4.wireOp",EDGE,"E9"),sQuery(id+"F5.wireOp",EDGE,"E10.0")])],"isStart":true}),makeQuery(id+"F18.opExtrude","CAP_FACE",FACE,{"disambiguationData":[OSD([sQuery(id+"F15.wireOp",EDGE,"E31"),sQuery(id+"F15.wireOp",EDGE,"E32"),sQuery(id+"F15.wireOp",EDGE,"E33"),sQuery(id+"F15.wireOp",EDGE,"E34"),sQuery(id+"F15.wireOp",EDGE,"E35"),sQuery(id+"F15.wireOp",EDGE,"E36")])],"isStart":true}),makeQuery(id+"F18.opExtrude","CAP_FACE",FACE,{"disambiguationData":[OSD([subQ0,sQuery(id+"F16.wireOp",EDGE,"E38"),sQuery(id+"F16.wireOp",EDGE,"E39"),sQuery(id+"F16.wireOp",EDGE,"E40")])],"isStart":true}),makeQuery(id+"F18.opExtrude","CAP_FACE",FACE,{"disambiguationData":[OSD([sQuery(id+"F17.wireOp",EDGE,"E41"),sQuery(id+"F17.wireOp",EDGE,"E42"),sQuery(id+"F17.wireOp",EDGE,"E43"),sQuery(id+"F17.wireOp",EDGE,"E44")])],"isStart":true}),makeQuery(id+"F18.opExtrude","CAP_FACE",FACE,{"disambiguationData":[OSD([sQuery(id+"F5.wireOp",EDGE,"E11.0")])],"isStart":true}),makeQuery(id+"F18.opExtrude","CAP_FACE",FACE,{"disambiguationData":[OSD([sQuery(id+"F5.wireOp",EDGE,"E12.0")])],"isStart":true})]})]});}
            var Q4;
            {var subQ1=sQuery(id+"F16.wireOp",EDGE,"E37");var subQ2=sQuery(id+"F5.wireOp",EDGE,"E12.0");Q4=makeQuery(id+"F21.opBoolean","SPLIT",EDGE,{"disambiguationData":[TD([makeQuery(id+"F18.opExtrude","SWEPT_FACE",FACE,{"disambiguationData":[OSD([subQ2])]})])],"derivedFrom":makeQuery(id+"F18.opExtrude","CAP_EDGE",EDGE,{"disambiguationData":[OSD([subQ1])],"isStart":true})});}
            var Q5;
            Q5=makeQuery(id+"F18.opExtrude","CAP_EDGE",EDGE,{"disambiguationData":[OSD([sQuery(id+"F5.wireOp",EDGE,"E12.0")])],"isStart":true});
            var Q6;
            {var subQ1=sQuery(id+"F5.wireOp",EDGE,"E12.0");var subQ2=sQuery(id+"F15.wireOp",EDGE,"E31");Q6=makeQuery(id+"F21.opBoolean","SPLIT",EDGE,{"disambiguationData":[TD([makeQuery(id+"F18.opExtrude","SWEPT_FACE",FACE,{"disambiguationData":[OSD([subQ1])]})])],"derivedFrom":makeQuery(id+"F18.opExtrude","CAP_EDGE",EDGE,{"disambiguationData":[OSD([subQ2])],"isStart":true})});}
            var Q7;
            {var subQ0=sQuery(id+"F15.wireOp",EDGE,"E31");var subQ1=sQuery(id+"F1.wireOp",EDGE,"E1.0");Q7=makeQuery(id+"F24.opFillet","BLEND_EDGE",EDGE,{"blendedFrom":[makeQuery(id+"F21.opBoolean","INTERSECT",EDGE,{"disambiguationData":[OD(1.0)],"derivedFrom":[makeQuery(id+"F18.opExtrude","SWEPT_FACE",FACE,{"disambiguationData":[OSD([subQ1])]}),makeQuery(id+"F18.opExtrude","SWEPT_FACE",FACE,{"disambiguationData":[OSD([subQ0])]})]}),makeQuery(id+"F21.opBoolean","MERGE",FACE,{"derivedFrom":[makeQuery(id+"F18.opExtrude","CAP_FACE",FACE,{"disambiguationData":[OSD([sQuery(id+"F0.wireOp",EDGE,"E0"),subQ1])],"isStart":true}),makeQuery(id+"F18.opExtrude","CAP_FACE",FACE,{"disambiguationData":[OSD([sQuery(id+"F4.wireOp",EDGE,"E9"),sQuery(id+"F5.wireOp",EDGE,"E10.0")])],"isStart":true}),makeQuery(id+"F18.opExtrude","CAP_FACE",FACE,{"disambiguationData":[OSD([subQ0,sQuery(id+"F15.wireOp",EDGE,"E32"),sQuery(id+"F15.wireOp",EDGE,"E33"),sQuery(id+"F15.wireOp",EDGE,"E34"),sQuery(id+"F15.wireOp",EDGE,"E35"),sQuery(id+"F15.wireOp",EDGE,"E36")])],"isStart":true}),makeQuery(id+"F18.opExtrude","CAP_FACE",FACE,{"disambiguationData":[OSD([sQuery(id+"F16.wireOp",EDGE,"E37"),sQuery(id+"F16.wireOp",EDGE,"E38"),sQuery(id+"F16.wireOp",EDGE,"E39"),sQuery(id+"F16.wireOp",EDGE,"E40")])],"isStart":true}),makeQuery(id+"F18.opExtrude","CAP_FACE",FACE,{"disambiguationData":[OSD([sQuery(id+"F17.wireOp",EDGE,"E41"),sQuery(id+"F17.wireOp",EDGE,"E42"),sQuery(id+"F17.wireOp",EDGE,"E43"),sQuery(id+"F17.wireOp",EDGE,"E44")])],"isStart":true}),makeQuery(id+"F18.opExtrude","CAP_FACE",FACE,{"disambiguationData":[OSD([sQuery(id+"F5.wireOp",EDGE,"E11.0")])],"isStart":true}),makeQuery(id+"F18.opExtrude","CAP_FACE",FACE,{"disambiguationData":[OSD([sQuery(id+"F5.wireOp",EDGE,"E12.0")])],"isStart":true})]})],"blendedInto":[makeQuery(id+"F21.opBoolean","MERGE",FACE,{"derivedFrom":[makeQuery(id+"F18.opExtrude","CAP_FACE",FACE,{"disambiguationData":[OSD([sQuery(id+"F0.wireOp",EDGE,"E0"),subQ1])],"isStart":true}),makeQuery(id+"F18.opExtrude","CAP_FACE",FACE,{"disambiguationData":[OSD([sQuery(id+"F4.wireOp",EDGE,"E9"),sQuery(id+"F5.wireOp",EDGE,"E10.0")])],"isStart":true}),makeQuery(id+"F18.opExtrude","CAP_FACE",FACE,{"disambiguationData":[OSD([subQ0,sQuery(id+"F15.wireOp",EDGE,"E32"),sQuery(id+"F15.wireOp",EDGE,"E33"),sQuery(id+"F15.wireOp",EDGE,"E34"),sQuery(id+"F15.wireOp",EDGE,"E35"),sQuery(id+"F15.wireOp",EDGE,"E36")])],"isStart":true}),makeQuery(id+"F18.opExtrude","CAP_FACE",FACE,{"disambiguationData":[OSD([sQuery(id+"F16.wireOp",EDGE,"E37"),sQuery(id+"F16.wireOp",EDGE,"E38"),sQuery(id+"F16.wireOp",EDGE,"E39"),sQuery(id+"F16.wireOp",EDGE,"E40")])],"isStart":true}),makeQuery(id+"F18.opExtrude","CAP_FACE",FACE,{"disambiguationData":[OSD([sQuery(id+"F17.wireOp",EDGE,"E41"),sQuery(id+"F17.wireOp",EDGE,"E42"),sQuery(id+"F17.wireOp",EDGE,"E43"),sQuery(id+"F17.wireOp",EDGE,"E44")])],"isStart":true}),makeQuery(id+"F18.opExtrude","CAP_FACE",FACE,{"disambiguationData":[OSD([sQuery(id+"F5.wireOp",EDGE,"E11.0")])],"isStart":true}),makeQuery(id+"F18.opExtrude","CAP_FACE",FACE,{"disambiguationData":[OSD([sQuery(id+"F5.wireOp",EDGE,"E12.0")])],"isStart":true})]})]});}
            var Q8;
            {var subQ0=sQuery(id+"F15.wireOp",EDGE,"E31");var subQ1=sQuery(id+"F1.wireOp",EDGE,"E1.0");Q8=makeQuery(id+"F24.opFillet","BLEND_EDGE",EDGE,{"blendedFrom":[makeQuery(id+"F21.opBoolean","INTERSECT",EDGE,{"disambiguationData":[OD(0.0)],"derivedFrom":[makeQuery(id+"F18.opExtrude","SWEPT_FACE",FACE,{"disambiguationData":[OSD([subQ1])]}),makeQuery(id+"F18.opExtrude","SWEPT_FACE",FACE,{"disambiguationData":[OSD([subQ0])]})]}),makeQuery(id+"F21.opBoolean","MERGE",FACE,{"derivedFrom":[makeQuery(id+"F18.opExtrude","CAP_FACE",FACE,{"disambiguationData":[OSD([sQuery(id+"F0.wireOp",EDGE,"E0"),subQ1])],"isStart":true}),makeQuery(id+"F18.opExtrude","CAP_FACE",FACE,{"disambiguationData":[OSD([sQuery(id+"F4.wireOp",EDGE,"E9"),sQuery(id+"F5.wireOp",EDGE,"E10.0")])],"isStart":true}),makeQuery(id+"F18.opExtrude","CAP_FACE",FACE,{"disambiguationData":[OSD([subQ0,sQuery(id+"F15.wireOp",EDGE,"E32"),sQuery(id+"F15.wireOp",EDGE,"E33"),sQuery(id+"F15.wireOp",EDGE,"E34"),sQuery(id+"F15.wireOp",EDGE,"E35"),sQuery(id+"F15.wireOp",EDGE,"E36")])],"isStart":true}),makeQuery(id+"F18.opExtrude","CAP_FACE",FACE,{"disambiguationData":[OSD([sQuery(id+"F16.wireOp",EDGE,"E37"),sQuery(id+"F16.wireOp",EDGE,"E38"),sQuery(id+"F16.wireOp",EDGE,"E39"),sQuery(id+"F16.wireOp",EDGE,"E40")])],"isStart":true}),makeQuery(id+"F18.opExtrude","CAP_FACE",FACE,{"disambiguationData":[OSD([sQuery(id+"F17.wireOp",EDGE,"E41"),sQuery(id+"F17.wireOp",EDGE,"E42"),sQuery(id+"F17.wireOp",EDGE,"E43"),sQuery(id+"F17.wireOp",EDGE,"E44")])],"isStart":true}),makeQuery(id+"F18.opExtrude","CAP_FACE",FACE,{"disambiguationData":[OSD([sQuery(id+"F5.wireOp",EDGE,"E11.0")])],"isStart":true}),makeQuery(id+"F18.opExtrude","CAP_FACE",FACE,{"disambiguationData":[OSD([sQuery(id+"F5.wireOp",EDGE,"E12.0")])],"isStart":true})]})],"blendedInto":[makeQuery(id+"F21.opBoolean","MERGE",FACE,{"derivedFrom":[makeQuery(id+"F18.opExtrude","CAP_FACE",FACE,{"disambiguationData":[OSD([sQuery(id+"F0.wireOp",EDGE,"E0"),subQ1])],"isStart":true}),makeQuery(id+"F18.opExtrude","CAP_FACE",FACE,{"disambiguationData":[OSD([sQuery(id+"F4.wireOp",EDGE,"E9"),sQuery(id+"F5.wireOp",EDGE,"E10.0")])],"isStart":true}),makeQuery(id+"F18.opExtrude","CAP_FACE",FACE,{"disambiguationData":[OSD([subQ0,sQuery(id+"F15.wireOp",EDGE,"E32"),sQuery(id+"F15.wireOp",EDGE,"E33"),sQuery(id+"F15.wireOp",EDGE,"E34"),sQuery(id+"F15.wireOp",EDGE,"E35"),sQuery(id+"F15.wireOp",EDGE,"E36")])],"isStart":true}),makeQuery(id+"F18.opExtrude","CAP_FACE",FACE,{"disambiguationData":[OSD([sQuery(id+"F16.wireOp",EDGE,"E37"),sQuery(id+"F16.wireOp",EDGE,"E38"),sQuery(id+"F16.wireOp",EDGE,"E39"),sQuery(id+"F16.wireOp",EDGE,"E40")])],"isStart":true}),makeQuery(id+"F18.opExtrude","CAP_FACE",FACE,{"disambiguationData":[OSD([sQuery(id+"F17.wireOp",EDGE,"E41"),sQuery(id+"F17.wireOp",EDGE,"E42"),sQuery(id+"F17.wireOp",EDGE,"E43"),sQuery(id+"F17.wireOp",EDGE,"E44")])],"isStart":true}),makeQuery(id+"F18.opExtrude","CAP_FACE",FACE,{"disambiguationData":[OSD([sQuery(id+"F5.wireOp",EDGE,"E11.0")])],"isStart":true}),makeQuery(id+"F18.opExtrude","CAP_FACE",FACE,{"disambiguationData":[OSD([sQuery(id+"F5.wireOp",EDGE,"E12.0")])],"isStart":true})]})]});}
            var Q9;
            {var subQ0=sQuery(id+"F5.wireOp",EDGE,"E10.0");var subQ1=sQuery(id+"F15.wireOp",EDGE,"E31");Q9=makeQuery(id+"F21.opBoolean","SPLIT",EDGE,{"disambiguationData":[TD([makeQuery(id+"F18.opExtrude","SWEPT_FACE",FACE,{"disambiguationData":[OSD([subQ0])]})])],"derivedFrom":makeQuery(id+"F18.opExtrude","CAP_EDGE",EDGE,{"disambiguationData":[OSD([subQ1])],"isStart":true})});}
            var Q10;
            Q10=makeQuery(id+"F18.opExtrude","CAP_EDGE",EDGE,{"disambiguationData":[OSD([sQuery(id+"F5.wireOp",EDGE,"E10.0")])],"isStart":true});
            var Q11;
            {var subQ0=sQuery(id+"F5.wireOp",EDGE,"E10.0");var subQ2=sQuery(id+"F17.wireOp",EDGE,"E41");Q11=makeQuery(id+"F21.opBoolean","SPLIT",EDGE,{"disambiguationData":[TD([makeQuery(id+"F18.opExtrude","SWEPT_FACE",FACE,{"disambiguationData":[OSD([subQ0])]})])],"derivedFrom":makeQuery(id+"F18.opExtrude","CAP_EDGE",EDGE,{"disambiguationData":[OSD([subQ2])],"isStart":true})});}
            var Q12;
            {var subQ0=sQuery(id+"F17.wireOp",EDGE,"E41");var subQ1=sQuery(id+"F1.wireOp",EDGE,"E1.0");Q12=makeQuery(id+"F23.opFillet","BLEND_EDGE",EDGE,{"blendedFrom":[makeQuery(id+"F21.opBoolean","INTERSECT",EDGE,{"disambiguationData":[OD(0.0)],"derivedFrom":[makeQuery(id+"F18.opExtrude","SWEPT_FACE",FACE,{"disambiguationData":[OSD([subQ1])]}),makeQuery(id+"F18.opExtrude","SWEPT_FACE",FACE,{"disambiguationData":[OSD([subQ0])]})]}),makeQuery(id+"F21.opBoolean","MERGE",FACE,{"derivedFrom":[makeQuery(id+"F18.opExtrude","CAP_FACE",FACE,{"disambiguationData":[OSD([sQuery(id+"F0.wireOp",EDGE,"E0"),subQ1])],"isStart":true}),makeQuery(id+"F18.opExtrude","CAP_FACE",FACE,{"disambiguationData":[OSD([sQuery(id+"F4.wireOp",EDGE,"E9"),sQuery(id+"F5.wireOp",EDGE,"E10.0")])],"isStart":true}),makeQuery(id+"F18.opExtrude","CAP_FACE",FACE,{"disambiguationData":[OSD([sQuery(id+"F15.wireOp",EDGE,"E31"),sQuery(id+"F15.wireOp",EDGE,"E32"),sQuery(id+"F15.wireOp",EDGE,"E33"),sQuery(id+"F15.wireOp",EDGE,"E34"),sQuery(id+"F15.wireOp",EDGE,"E35"),sQuery(id+"F15.wireOp",EDGE,"E36")])],"isStart":true}),makeQuery(id+"F18.opExtrude","CAP_FACE",FACE,{"disambiguationData":[OSD([sQuery(id+"F16.wireOp",EDGE,"E37"),sQuery(id+"F16.wireOp",EDGE,"E38"),sQuery(id+"F16.wireOp",EDGE,"E39"),sQuery(id+"F16.wireOp",EDGE,"E40")])],"isStart":true}),makeQuery(id+"F18.opExtrude","CAP_FACE",FACE,{"disambiguationData":[OSD([subQ0,sQuery(id+"F17.wireOp",EDGE,"E42"),sQuery(id+"F17.wireOp",EDGE,"E43"),sQuery(id+"F17.wireOp",EDGE,"E44")])],"isStart":true}),makeQuery(id+"F18.opExtrude","CAP_FACE",FACE,{"disambiguationData":[OSD([sQuery(id+"F5.wireOp",EDGE,"E11.0")])],"isStart":true}),makeQuery(id+"F18.opExtrude","CAP_FACE",FACE,{"disambiguationData":[OSD([sQuery(id+"F5.wireOp",EDGE,"E12.0")])],"isStart":true})]})],"blendedInto":[makeQuery(id+"F21.opBoolean","MERGE",FACE,{"derivedFrom":[makeQuery(id+"F18.opExtrude","CAP_FACE",FACE,{"disambiguationData":[OSD([sQuery(id+"F0.wireOp",EDGE,"E0"),subQ1])],"isStart":true}),makeQuery(id+"F18.opExtrude","CAP_FACE",FACE,{"disambiguationData":[OSD([sQuery(id+"F4.wireOp",EDGE,"E9"),sQuery(id+"F5.wireOp",EDGE,"E10.0")])],"isStart":true}),makeQuery(id+"F18.opExtrude","CAP_FACE",FACE,{"disambiguationData":[OSD([sQuery(id+"F15.wireOp",EDGE,"E31"),sQuery(id+"F15.wireOp",EDGE,"E32"),sQuery(id+"F15.wireOp",EDGE,"E33"),sQuery(id+"F15.wireOp",EDGE,"E34"),sQuery(id+"F15.wireOp",EDGE,"E35"),sQuery(id+"F15.wireOp",EDGE,"E36")])],"isStart":true}),makeQuery(id+"F18.opExtrude","CAP_FACE",FACE,{"disambiguationData":[OSD([sQuery(id+"F16.wireOp",EDGE,"E37"),sQuery(id+"F16.wireOp",EDGE,"E38"),sQuery(id+"F16.wireOp",EDGE,"E39"),sQuery(id+"F16.wireOp",EDGE,"E40")])],"isStart":true}),makeQuery(id+"F18.opExtrude","CAP_FACE",FACE,{"disambiguationData":[OSD([subQ0,sQuery(id+"F17.wireOp",EDGE,"E42"),sQuery(id+"F17.wireOp",EDGE,"E43"),sQuery(id+"F17.wireOp",EDGE,"E44")])],"isStart":true}),makeQuery(id+"F18.opExtrude","CAP_FACE",FACE,{"disambiguationData":[OSD([sQuery(id+"F5.wireOp",EDGE,"E11.0")])],"isStart":true}),makeQuery(id+"F18.opExtrude","CAP_FACE",FACE,{"disambiguationData":[OSD([sQuery(id+"F5.wireOp",EDGE,"E12.0")])],"isStart":true})]})]});}
            var Q13;
            {var subQ0=sQuery(id+"F17.wireOp",EDGE,"E41");var subQ1=sQuery(id+"F1.wireOp",EDGE,"E1.0");Q13=makeQuery(id+"F23.opFillet","BLEND_EDGE",EDGE,{"blendedFrom":[makeQuery(id+"F21.opBoolean","INTERSECT",EDGE,{"disambiguationData":[OD(1.0)],"derivedFrom":[makeQuery(id+"F18.opExtrude","SWEPT_FACE",FACE,{"disambiguationData":[OSD([subQ1])]}),makeQuery(id+"F18.opExtrude","SWEPT_FACE",FACE,{"disambiguationData":[OSD([subQ0])]})]}),makeQuery(id+"F21.opBoolean","MERGE",FACE,{"derivedFrom":[makeQuery(id+"F18.opExtrude","CAP_FACE",FACE,{"disambiguationData":[OSD([sQuery(id+"F0.wireOp",EDGE,"E0"),subQ1])],"isStart":true}),makeQuery(id+"F18.opExtrude","CAP_FACE",FACE,{"disambiguationData":[OSD([sQuery(id+"F4.wireOp",EDGE,"E9"),sQuery(id+"F5.wireOp",EDGE,"E10.0")])],"isStart":true}),makeQuery(id+"F18.opExtrude","CAP_FACE",FACE,{"disambiguationData":[OSD([sQuery(id+"F15.wireOp",EDGE,"E31"),sQuery(id+"F15.wireOp",EDGE,"E32"),sQuery(id+"F15.wireOp",EDGE,"E33"),sQuery(id+"F15.wireOp",EDGE,"E34"),sQuery(id+"F15.wireOp",EDGE,"E35"),sQuery(id+"F15.wireOp",EDGE,"E36")])],"isStart":true}),makeQuery(id+"F18.opExtrude","CAP_FACE",FACE,{"disambiguationData":[OSD([sQuery(id+"F16.wireOp",EDGE,"E37"),sQuery(id+"F16.wireOp",EDGE,"E38"),sQuery(id+"F16.wireOp",EDGE,"E39"),sQuery(id+"F16.wireOp",EDGE,"E40")])],"isStart":true}),makeQuery(id+"F18.opExtrude","CAP_FACE",FACE,{"disambiguationData":[OSD([subQ0,sQuery(id+"F17.wireOp",EDGE,"E42"),sQuery(id+"F17.wireOp",EDGE,"E43"),sQuery(id+"F17.wireOp",EDGE,"E44")])],"isStart":true}),makeQuery(id+"F18.opExtrude","CAP_FACE",FACE,{"disambiguationData":[OSD([sQuery(id+"F5.wireOp",EDGE,"E11.0")])],"isStart":true}),makeQuery(id+"F18.opExtrude","CAP_FACE",FACE,{"disambiguationData":[OSD([sQuery(id+"F5.wireOp",EDGE,"E12.0")])],"isStart":true})]})],"blendedInto":[makeQuery(id+"F21.opBoolean","MERGE",FACE,{"derivedFrom":[makeQuery(id+"F18.opExtrude","CAP_FACE",FACE,{"disambiguationData":[OSD([sQuery(id+"F0.wireOp",EDGE,"E0"),subQ1])],"isStart":true}),makeQuery(id+"F18.opExtrude","CAP_FACE",FACE,{"disambiguationData":[OSD([sQuery(id+"F4.wireOp",EDGE,"E9"),sQuery(id+"F5.wireOp",EDGE,"E10.0")])],"isStart":true}),makeQuery(id+"F18.opExtrude","CAP_FACE",FACE,{"disambiguationData":[OSD([sQuery(id+"F15.wireOp",EDGE,"E31"),sQuery(id+"F15.wireOp",EDGE,"E32"),sQuery(id+"F15.wireOp",EDGE,"E33"),sQuery(id+"F15.wireOp",EDGE,"E34"),sQuery(id+"F15.wireOp",EDGE,"E35"),sQuery(id+"F15.wireOp",EDGE,"E36")])],"isStart":true}),makeQuery(id+"F18.opExtrude","CAP_FACE",FACE,{"disambiguationData":[OSD([sQuery(id+"F16.wireOp",EDGE,"E37"),sQuery(id+"F16.wireOp",EDGE,"E38"),sQuery(id+"F16.wireOp",EDGE,"E39"),sQuery(id+"F16.wireOp",EDGE,"E40")])],"isStart":true}),makeQuery(id+"F18.opExtrude","CAP_FACE",FACE,{"disambiguationData":[OSD([subQ0,sQuery(id+"F17.wireOp",EDGE,"E42"),sQuery(id+"F17.wireOp",EDGE,"E43"),sQuery(id+"F17.wireOp",EDGE,"E44")])],"isStart":true}),makeQuery(id+"F18.opExtrude","CAP_FACE",FACE,{"disambiguationData":[OSD([sQuery(id+"F5.wireOp",EDGE,"E11.0")])],"isStart":true}),makeQuery(id+"F18.opExtrude","CAP_FACE",FACE,{"disambiguationData":[OSD([sQuery(id+"F5.wireOp",EDGE,"E12.0")])],"isStart":true})]})]});}
            var Q14;
            {var subQ0=sQuery(id+"F5.wireOp",EDGE,"E11.0");var subQ1=sQuery(id+"F17.wireOp",EDGE,"E41");Q14=makeQuery(id+"F21.opBoolean","SPLIT",EDGE,{"disambiguationData":[TD([makeQuery(id+"F18.opExtrude","SWEPT_FACE",FACE,{"disambiguationData":[OSD([subQ0])]})])],"derivedFrom":makeQuery(id+"F18.opExtrude","CAP_EDGE",EDGE,{"disambiguationData":[OSD([subQ1])],"isStart":true})});}
            chamfer(context, id + "F28", {"entities" : qUnion([Q0, Q1, Q2, Q3, Q4, Q5, Q6, Q7, Q8, Q9, Q10, Q11, Q12, Q13, Q14]), "width" : 1 * mm, "tangentPropagation" : true});
        }
        {
            var Q0;
            {var subQ2=sQuery(id+"F5.wireOp",EDGE,"E10.0");var subQ8=sQuery(id+"F17.wireOp",EDGE,"E41");var subQ20=makeQuery(id+"F18.opExtrude","SWEPT_FACE",FACE,{"disambiguationData":[OSD([subQ2])]});var subQ29=makeQuery(id+"F18.opExtrude","SWEPT_FACE",FACE,{"disambiguationData":[OSD([subQ8])]});Q0=makeQuery(id+"F27.opChamfer","BLEND_EDGE",EDGE,{"blendedFrom":[makeQuery(id+"F21.opBoolean","SPLIT",EDGE,{"disambiguationData":[TD([subQ20])],"derivedFrom":makeQuery(id+"F18.opExtrude","CAP_EDGE",EDGE,{"disambiguationData":[OSD([subQ8])],"isStart":false})}),makeQuery(id+"F21.opBoolean","SPLIT",FACE,{"disambiguationData":[TD([subQ20])],"derivedFrom":subQ29})],"blendedInto":[makeQuery(id+"F21.opBoolean","SPLIT",FACE,{"disambiguationData":[TD([subQ20])],"derivedFrom":subQ29})]});}
            var Q1;
            {var subQ0=sQuery(id+"F17.wireOp",EDGE,"E41");var subQ1=sQuery(id+"F1.wireOp",EDGE,"E1.0");var subQ2=makeQuery(id+"F21.opBoolean","INTERSECT",EDGE,{"disambiguationData":[OD(0.0)],"derivedFrom":[makeQuery(id+"F18.opExtrude","SWEPT_FACE",FACE,{"disambiguationData":[OSD([subQ1])]}),makeQuery(id+"F18.opExtrude","SWEPT_FACE",FACE,{"disambiguationData":[OSD([subQ0])]})]});Q1=makeQuery(id+"F27.opChamfer","BLEND_EDGE",EDGE,{"blendedFrom":[makeQuery(id+"F23.opFillet","BLEND_EDGE",EDGE,{"blendedFrom":[subQ2,makeQuery(id+"F21.opBoolean","MERGE",FACE,{"derivedFrom":[makeQuery(id+"F18.opExtrude","CAP_FACE",FACE,{"disambiguationData":[OSD([sQuery(id+"F0.wireOp",EDGE,"E0"),subQ1])],"isStart":false}),makeQuery(id+"F18.opExtrude","CAP_FACE",FACE,{"disambiguationData":[OSD([sQuery(id+"F4.wireOp",EDGE,"E9"),sQuery(id+"F5.wireOp",EDGE,"E10.0")])],"isStart":false}),makeQuery(id+"F18.opExtrude","CAP_FACE",FACE,{"disambiguationData":[OSD([sQuery(id+"F15.wireOp",EDGE,"E31"),sQuery(id+"F15.wireOp",EDGE,"E32"),sQuery(id+"F15.wireOp",EDGE,"E33"),sQuery(id+"F15.wireOp",EDGE,"E34"),sQuery(id+"F15.wireOp",EDGE,"E35"),sQuery(id+"F15.wireOp",EDGE,"E36")])],"isStart":false}),makeQuery(id+"F18.opExtrude","CAP_FACE",FACE,{"disambiguationData":[OSD([sQuery(id+"F16.wireOp",EDGE,"E37"),sQuery(id+"F16.wireOp",EDGE,"E38"),sQuery(id+"F16.wireOp",EDGE,"E39"),sQuery(id+"F16.wireOp",EDGE,"E40")])],"isStart":false}),makeQuery(id+"F18.opExtrude","CAP_FACE",FACE,{"disambiguationData":[OSD([subQ0,sQuery(id+"F17.wireOp",EDGE,"E42"),sQuery(id+"F17.wireOp",EDGE,"E43"),sQuery(id+"F17.wireOp",EDGE,"E44")])],"isStart":false}),makeQuery(id+"F18.opExtrude","CAP_FACE",FACE,{"disambiguationData":[OSD([sQuery(id+"F5.wireOp",EDGE,"E11.0")])],"isStart":false}),makeQuery(id+"F18.opExtrude","CAP_FACE",FACE,{"disambiguationData":[OSD([sQuery(id+"F5.wireOp",EDGE,"E12.0")])],"isStart":false})]})],"blendedInto":[makeQuery(id+"F21.opBoolean","MERGE",FACE,{"derivedFrom":[makeQuery(id+"F18.opExtrude","CAP_FACE",FACE,{"disambiguationData":[OSD([sQuery(id+"F0.wireOp",EDGE,"E0"),subQ1])],"isStart":false}),makeQuery(id+"F18.opExtrude","CAP_FACE",FACE,{"disambiguationData":[OSD([sQuery(id+"F4.wireOp",EDGE,"E9"),sQuery(id+"F5.wireOp",EDGE,"E10.0")])],"isStart":false}),makeQuery(id+"F18.opExtrude","CAP_FACE",FACE,{"disambiguationData":[OSD([sQuery(id+"F15.wireOp",EDGE,"E31"),sQuery(id+"F15.wireOp",EDGE,"E32"),sQuery(id+"F15.wireOp",EDGE,"E33"),sQuery(id+"F15.wireOp",EDGE,"E34"),sQuery(id+"F15.wireOp",EDGE,"E35"),sQuery(id+"F15.wireOp",EDGE,"E36")])],"isStart":false}),makeQuery(id+"F18.opExtrude","CAP_FACE",FACE,{"disambiguationData":[OSD([sQuery(id+"F16.wireOp",EDGE,"E37"),sQuery(id+"F16.wireOp",EDGE,"E38"),sQuery(id+"F16.wireOp",EDGE,"E39"),sQuery(id+"F16.wireOp",EDGE,"E40")])],"isStart":false}),makeQuery(id+"F18.opExtrude","CAP_FACE",FACE,{"disambiguationData":[OSD([subQ0,sQuery(id+"F17.wireOp",EDGE,"E42"),sQuery(id+"F17.wireOp",EDGE,"E43"),sQuery(id+"F17.wireOp",EDGE,"E44")])],"isStart":false}),makeQuery(id+"F18.opExtrude","CAP_FACE",FACE,{"disambiguationData":[OSD([sQuery(id+"F5.wireOp",EDGE,"E11.0")])],"isStart":false}),makeQuery(id+"F18.opExtrude","CAP_FACE",FACE,{"disambiguationData":[OSD([sQuery(id+"F5.wireOp",EDGE,"E12.0")])],"isStart":false})]})]}),makeQuery(id+"F23.opFillet","BLEND_FACE",FACE,{"disambiguationData":[OSD([subQ1,subQ0]),TDD([subQ2])]})],"blendedInto":[makeQuery(id+"F23.opFillet","BLEND_FACE",FACE,{"disambiguationData":[OSD([subQ1,subQ0]),TDD([subQ2])]})]});}
            var Q2;
            {var subQ0=sQuery(id+"F17.wireOp",EDGE,"E41");var subQ1=sQuery(id+"F1.wireOp",EDGE,"E1.0");var subQ2=makeQuery(id+"F21.opBoolean","INTERSECT",EDGE,{"disambiguationData":[OD(1.0)],"derivedFrom":[makeQuery(id+"F18.opExtrude","SWEPT_FACE",FACE,{"disambiguationData":[OSD([subQ1])]}),makeQuery(id+"F18.opExtrude","SWEPT_FACE",FACE,{"disambiguationData":[OSD([subQ0])]})]});Q2=makeQuery(id+"F27.opChamfer","BLEND_EDGE",EDGE,{"blendedFrom":[makeQuery(id+"F23.opFillet","BLEND_EDGE",EDGE,{"blendedFrom":[subQ2,makeQuery(id+"F21.opBoolean","MERGE",FACE,{"derivedFrom":[makeQuery(id+"F18.opExtrude","CAP_FACE",FACE,{"disambiguationData":[OSD([sQuery(id+"F0.wireOp",EDGE,"E0"),subQ1])],"isStart":false}),makeQuery(id+"F18.opExtrude","CAP_FACE",FACE,{"disambiguationData":[OSD([sQuery(id+"F4.wireOp",EDGE,"E9"),sQuery(id+"F5.wireOp",EDGE,"E10.0")])],"isStart":false}),makeQuery(id+"F18.opExtrude","CAP_FACE",FACE,{"disambiguationData":[OSD([sQuery(id+"F15.wireOp",EDGE,"E31"),sQuery(id+"F15.wireOp",EDGE,"E32"),sQuery(id+"F15.wireOp",EDGE,"E33"),sQuery(id+"F15.wireOp",EDGE,"E34"),sQuery(id+"F15.wireOp",EDGE,"E35"),sQuery(id+"F15.wireOp",EDGE,"E36")])],"isStart":false}),makeQuery(id+"F18.opExtrude","CAP_FACE",FACE,{"disambiguationData":[OSD([sQuery(id+"F16.wireOp",EDGE,"E37"),sQuery(id+"F16.wireOp",EDGE,"E38"),sQuery(id+"F16.wireOp",EDGE,"E39"),sQuery(id+"F16.wireOp",EDGE,"E40")])],"isStart":false}),makeQuery(id+"F18.opExtrude","CAP_FACE",FACE,{"disambiguationData":[OSD([subQ0,sQuery(id+"F17.wireOp",EDGE,"E42"),sQuery(id+"F17.wireOp",EDGE,"E43"),sQuery(id+"F17.wireOp",EDGE,"E44")])],"isStart":false}),makeQuery(id+"F18.opExtrude","CAP_FACE",FACE,{"disambiguationData":[OSD([sQuery(id+"F5.wireOp",EDGE,"E11.0")])],"isStart":false}),makeQuery(id+"F18.opExtrude","CAP_FACE",FACE,{"disambiguationData":[OSD([sQuery(id+"F5.wireOp",EDGE,"E12.0")])],"isStart":false})]})],"blendedInto":[makeQuery(id+"F21.opBoolean","MERGE",FACE,{"derivedFrom":[makeQuery(id+"F18.opExtrude","CAP_FACE",FACE,{"disambiguationData":[OSD([sQuery(id+"F0.wireOp",EDGE,"E0"),subQ1])],"isStart":false}),makeQuery(id+"F18.opExtrude","CAP_FACE",FACE,{"disambiguationData":[OSD([sQuery(id+"F4.wireOp",EDGE,"E9"),sQuery(id+"F5.wireOp",EDGE,"E10.0")])],"isStart":false}),makeQuery(id+"F18.opExtrude","CAP_FACE",FACE,{"disambiguationData":[OSD([sQuery(id+"F15.wireOp",EDGE,"E31"),sQuery(id+"F15.wireOp",EDGE,"E32"),sQuery(id+"F15.wireOp",EDGE,"E33"),sQuery(id+"F15.wireOp",EDGE,"E34"),sQuery(id+"F15.wireOp",EDGE,"E35"),sQuery(id+"F15.wireOp",EDGE,"E36")])],"isStart":false}),makeQuery(id+"F18.opExtrude","CAP_FACE",FACE,{"disambiguationData":[OSD([sQuery(id+"F16.wireOp",EDGE,"E37"),sQuery(id+"F16.wireOp",EDGE,"E38"),sQuery(id+"F16.wireOp",EDGE,"E39"),sQuery(id+"F16.wireOp",EDGE,"E40")])],"isStart":false}),makeQuery(id+"F18.opExtrude","CAP_FACE",FACE,{"disambiguationData":[OSD([subQ0,sQuery(id+"F17.wireOp",EDGE,"E42"),sQuery(id+"F17.wireOp",EDGE,"E43"),sQuery(id+"F17.wireOp",EDGE,"E44")])],"isStart":false}),makeQuery(id+"F18.opExtrude","CAP_FACE",FACE,{"disambiguationData":[OSD([sQuery(id+"F5.wireOp",EDGE,"E11.0")])],"isStart":false}),makeQuery(id+"F18.opExtrude","CAP_FACE",FACE,{"disambiguationData":[OSD([sQuery(id+"F5.wireOp",EDGE,"E12.0")])],"isStart":false})]})]}),makeQuery(id+"F23.opFillet","BLEND_FACE",FACE,{"disambiguationData":[OSD([subQ1,subQ0]),TDD([subQ2])]})],"blendedInto":[makeQuery(id+"F23.opFillet","BLEND_FACE",FACE,{"disambiguationData":[OSD([subQ1,subQ0]),TDD([subQ2])]})]});}
            var Q3;
            {var subQ0=sQuery(id+"F5.wireOp",EDGE,"E11.0");var subQ2=makeQuery(id+"F18.opExtrude","SWEPT_FACE",FACE,{"disambiguationData":[OSD([subQ0])]});var subQ6=sQuery(id+"F17.wireOp",EDGE,"E41");var subQ29=makeQuery(id+"F18.opExtrude","SWEPT_FACE",FACE,{"disambiguationData":[OSD([subQ6])]});Q3=makeQuery(id+"F27.opChamfer","BLEND_EDGE",EDGE,{"blendedFrom":[makeQuery(id+"F21.opBoolean","SPLIT",EDGE,{"disambiguationData":[TD([subQ2])],"derivedFrom":makeQuery(id+"F18.opExtrude","CAP_EDGE",EDGE,{"disambiguationData":[OSD([subQ6])],"isStart":false})}),makeQuery(id+"F21.opBoolean","SPLIT",FACE,{"disambiguationData":[TD([subQ2])],"derivedFrom":subQ29})],"blendedInto":[makeQuery(id+"F21.opBoolean","SPLIT",FACE,{"disambiguationData":[TD([subQ2])],"derivedFrom":subQ29})]});}
            var Q4;
            {var subQ0=sQuery(id+"F5.wireOp",EDGE,"E11.0");Q4=makeQuery(id+"F27.opChamfer","BLEND_EDGE",EDGE,{"blendedFrom":[makeQuery(id+"F18.opExtrude","CAP_EDGE",EDGE,{"disambiguationData":[OSD([subQ0])],"isStart":false}),makeQuery(id+"F18.opExtrude","SWEPT_FACE",FACE,{"disambiguationData":[OSD([subQ0])]})],"blendedInto":[makeQuery(id+"F18.opExtrude","SWEPT_FACE",FACE,{"disambiguationData":[OSD([subQ0])]})]});}
            var Q5;
            {var subQ0=sQuery(id+"F5.wireOp",EDGE,"E10.0");Q5=makeQuery(id+"F27.opChamfer","BLEND_EDGE",EDGE,{"blendedFrom":[makeQuery(id+"F18.opExtrude","CAP_EDGE",EDGE,{"disambiguationData":[OSD([subQ0])],"isStart":false}),makeQuery(id+"F18.opExtrude","SWEPT_FACE",FACE,{"disambiguationData":[OSD([subQ0])]})],"blendedInto":[makeQuery(id+"F18.opExtrude","SWEPT_FACE",FACE,{"disambiguationData":[OSD([subQ0])]})]});}
            var Q6;
            {var subQ0=sQuery(id+"F5.wireOp",EDGE,"E11.0");Q6=makeQuery(id+"F28.opChamfer","BLEND_EDGE",EDGE,{"blendedFrom":[makeQuery(id+"F18.opExtrude","CAP_EDGE",EDGE,{"disambiguationData":[OSD([subQ0])],"isStart":true}),makeQuery(id+"F18.opExtrude","SWEPT_FACE",FACE,{"disambiguationData":[OSD([subQ0])]})],"blendedInto":[makeQuery(id+"F18.opExtrude","SWEPT_FACE",FACE,{"disambiguationData":[OSD([subQ0])]})]});}
            var Q7;
            {var subQ0=sQuery(id+"F5.wireOp",EDGE,"E11.0");var subQ2=makeQuery(id+"F18.opExtrude","SWEPT_FACE",FACE,{"disambiguationData":[OSD([subQ0])]});var subQ6=sQuery(id+"F17.wireOp",EDGE,"E41");var subQ29=makeQuery(id+"F18.opExtrude","SWEPT_FACE",FACE,{"disambiguationData":[OSD([subQ6])]});Q7=makeQuery(id+"F28.opChamfer","BLEND_EDGE",EDGE,{"blendedFrom":[makeQuery(id+"F21.opBoolean","SPLIT",EDGE,{"disambiguationData":[TD([subQ2])],"derivedFrom":makeQuery(id+"F18.opExtrude","CAP_EDGE",EDGE,{"disambiguationData":[OSD([subQ6])],"isStart":true})}),makeQuery(id+"F21.opBoolean","SPLIT",FACE,{"disambiguationData":[TD([subQ2])],"derivedFrom":subQ29})],"blendedInto":[makeQuery(id+"F21.opBoolean","SPLIT",FACE,{"disambiguationData":[TD([subQ2])],"derivedFrom":subQ29})]});}
            var Q8;
            {var subQ0=sQuery(id+"F17.wireOp",EDGE,"E41");var subQ1=sQuery(id+"F1.wireOp",EDGE,"E1.0");var subQ2=makeQuery(id+"F21.opBoolean","INTERSECT",EDGE,{"disambiguationData":[OD(1.0)],"derivedFrom":[makeQuery(id+"F18.opExtrude","SWEPT_FACE",FACE,{"disambiguationData":[OSD([subQ1])]}),makeQuery(id+"F18.opExtrude","SWEPT_FACE",FACE,{"disambiguationData":[OSD([subQ0])]})]});Q8=makeQuery(id+"F28.opChamfer","BLEND_EDGE",EDGE,{"blendedFrom":[makeQuery(id+"F23.opFillet","BLEND_EDGE",EDGE,{"blendedFrom":[subQ2,makeQuery(id+"F21.opBoolean","MERGE",FACE,{"derivedFrom":[makeQuery(id+"F18.opExtrude","CAP_FACE",FACE,{"disambiguationData":[OSD([sQuery(id+"F0.wireOp",EDGE,"E0"),subQ1])],"isStart":true}),makeQuery(id+"F18.opExtrude","CAP_FACE",FACE,{"disambiguationData":[OSD([sQuery(id+"F4.wireOp",EDGE,"E9"),sQuery(id+"F5.wireOp",EDGE,"E10.0")])],"isStart":true}),makeQuery(id+"F18.opExtrude","CAP_FACE",FACE,{"disambiguationData":[OSD([sQuery(id+"F15.wireOp",EDGE,"E31"),sQuery(id+"F15.wireOp",EDGE,"E32"),sQuery(id+"F15.wireOp",EDGE,"E33"),sQuery(id+"F15.wireOp",EDGE,"E34"),sQuery(id+"F15.wireOp",EDGE,"E35"),sQuery(id+"F15.wireOp",EDGE,"E36")])],"isStart":true}),makeQuery(id+"F18.opExtrude","CAP_FACE",FACE,{"disambiguationData":[OSD([sQuery(id+"F16.wireOp",EDGE,"E37"),sQuery(id+"F16.wireOp",EDGE,"E38"),sQuery(id+"F16.wireOp",EDGE,"E39"),sQuery(id+"F16.wireOp",EDGE,"E40")])],"isStart":true}),makeQuery(id+"F18.opExtrude","CAP_FACE",FACE,{"disambiguationData":[OSD([subQ0,sQuery(id+"F17.wireOp",EDGE,"E42"),sQuery(id+"F17.wireOp",EDGE,"E43"),sQuery(id+"F17.wireOp",EDGE,"E44")])],"isStart":true}),makeQuery(id+"F18.opExtrude","CAP_FACE",FACE,{"disambiguationData":[OSD([sQuery(id+"F5.wireOp",EDGE,"E11.0")])],"isStart":true}),makeQuery(id+"F18.opExtrude","CAP_FACE",FACE,{"disambiguationData":[OSD([sQuery(id+"F5.wireOp",EDGE,"E12.0")])],"isStart":true})]})],"blendedInto":[makeQuery(id+"F21.opBoolean","MERGE",FACE,{"derivedFrom":[makeQuery(id+"F18.opExtrude","CAP_FACE",FACE,{"disambiguationData":[OSD([sQuery(id+"F0.wireOp",EDGE,"E0"),subQ1])],"isStart":true}),makeQuery(id+"F18.opExtrude","CAP_FACE",FACE,{"disambiguationData":[OSD([sQuery(id+"F4.wireOp",EDGE,"E9"),sQuery(id+"F5.wireOp",EDGE,"E10.0")])],"isStart":true}),makeQuery(id+"F18.opExtrude","CAP_FACE",FACE,{"disambiguationData":[OSD([sQuery(id+"F15.wireOp",EDGE,"E31"),sQuery(id+"F15.wireOp",EDGE,"E32"),sQuery(id+"F15.wireOp",EDGE,"E33"),sQuery(id+"F15.wireOp",EDGE,"E34"),sQuery(id+"F15.wireOp",EDGE,"E35"),sQuery(id+"F15.wireOp",EDGE,"E36")])],"isStart":true}),makeQuery(id+"F18.opExtrude","CAP_FACE",FACE,{"disambiguationData":[OSD([sQuery(id+"F16.wireOp",EDGE,"E37"),sQuery(id+"F16.wireOp",EDGE,"E38"),sQuery(id+"F16.wireOp",EDGE,"E39"),sQuery(id+"F16.wireOp",EDGE,"E40")])],"isStart":true}),makeQuery(id+"F18.opExtrude","CAP_FACE",FACE,{"disambiguationData":[OSD([subQ0,sQuery(id+"F17.wireOp",EDGE,"E42"),sQuery(id+"F17.wireOp",EDGE,"E43"),sQuery(id+"F17.wireOp",EDGE,"E44")])],"isStart":true}),makeQuery(id+"F18.opExtrude","CAP_FACE",FACE,{"disambiguationData":[OSD([sQuery(id+"F5.wireOp",EDGE,"E11.0")])],"isStart":true}),makeQuery(id+"F18.opExtrude","CAP_FACE",FACE,{"disambiguationData":[OSD([sQuery(id+"F5.wireOp",EDGE,"E12.0")])],"isStart":true})]})]}),makeQuery(id+"F23.opFillet","BLEND_FACE",FACE,{"disambiguationData":[OSD([subQ1,subQ0]),TDD([subQ2])]})],"blendedInto":[makeQuery(id+"F23.opFillet","BLEND_FACE",FACE,{"disambiguationData":[OSD([subQ1,subQ0]),TDD([subQ2])]})]});}
            var Q9;
            {var subQ0=sQuery(id+"F17.wireOp",EDGE,"E41");var subQ1=sQuery(id+"F1.wireOp",EDGE,"E1.0");var subQ2=makeQuery(id+"F21.opBoolean","INTERSECT",EDGE,{"disambiguationData":[OD(0.0)],"derivedFrom":[makeQuery(id+"F18.opExtrude","SWEPT_FACE",FACE,{"disambiguationData":[OSD([subQ1])]}),makeQuery(id+"F18.opExtrude","SWEPT_FACE",FACE,{"disambiguationData":[OSD([subQ0])]})]});Q9=makeQuery(id+"F28.opChamfer","BLEND_EDGE",EDGE,{"blendedFrom":[makeQuery(id+"F23.opFillet","BLEND_EDGE",EDGE,{"blendedFrom":[subQ2,makeQuery(id+"F21.opBoolean","MERGE",FACE,{"derivedFrom":[makeQuery(id+"F18.opExtrude","CAP_FACE",FACE,{"disambiguationData":[OSD([sQuery(id+"F0.wireOp",EDGE,"E0"),subQ1])],"isStart":true}),makeQuery(id+"F18.opExtrude","CAP_FACE",FACE,{"disambiguationData":[OSD([sQuery(id+"F4.wireOp",EDGE,"E9"),sQuery(id+"F5.wireOp",EDGE,"E10.0")])],"isStart":true}),makeQuery(id+"F18.opExtrude","CAP_FACE",FACE,{"disambiguationData":[OSD([sQuery(id+"F15.wireOp",EDGE,"E31"),sQuery(id+"F15.wireOp",EDGE,"E32"),sQuery(id+"F15.wireOp",EDGE,"E33"),sQuery(id+"F15.wireOp",EDGE,"E34"),sQuery(id+"F15.wireOp",EDGE,"E35"),sQuery(id+"F15.wireOp",EDGE,"E36")])],"isStart":true}),makeQuery(id+"F18.opExtrude","CAP_FACE",FACE,{"disambiguationData":[OSD([sQuery(id+"F16.wireOp",EDGE,"E37"),sQuery(id+"F16.wireOp",EDGE,"E38"),sQuery(id+"F16.wireOp",EDGE,"E39"),sQuery(id+"F16.wireOp",EDGE,"E40")])],"isStart":true}),makeQuery(id+"F18.opExtrude","CAP_FACE",FACE,{"disambiguationData":[OSD([subQ0,sQuery(id+"F17.wireOp",EDGE,"E42"),sQuery(id+"F17.wireOp",EDGE,"E43"),sQuery(id+"F17.wireOp",EDGE,"E44")])],"isStart":true}),makeQuery(id+"F18.opExtrude","CAP_FACE",FACE,{"disambiguationData":[OSD([sQuery(id+"F5.wireOp",EDGE,"E11.0")])],"isStart":true}),makeQuery(id+"F18.opExtrude","CAP_FACE",FACE,{"disambiguationData":[OSD([sQuery(id+"F5.wireOp",EDGE,"E12.0")])],"isStart":true})]})],"blendedInto":[makeQuery(id+"F21.opBoolean","MERGE",FACE,{"derivedFrom":[makeQuery(id+"F18.opExtrude","CAP_FACE",FACE,{"disambiguationData":[OSD([sQuery(id+"F0.wireOp",EDGE,"E0"),subQ1])],"isStart":true}),makeQuery(id+"F18.opExtrude","CAP_FACE",FACE,{"disambiguationData":[OSD([sQuery(id+"F4.wireOp",EDGE,"E9"),sQuery(id+"F5.wireOp",EDGE,"E10.0")])],"isStart":true}),makeQuery(id+"F18.opExtrude","CAP_FACE",FACE,{"disambiguationData":[OSD([sQuery(id+"F15.wireOp",EDGE,"E31"),sQuery(id+"F15.wireOp",EDGE,"E32"),sQuery(id+"F15.wireOp",EDGE,"E33"),sQuery(id+"F15.wireOp",EDGE,"E34"),sQuery(id+"F15.wireOp",EDGE,"E35"),sQuery(id+"F15.wireOp",EDGE,"E36")])],"isStart":true}),makeQuery(id+"F18.opExtrude","CAP_FACE",FACE,{"disambiguationData":[OSD([sQuery(id+"F16.wireOp",EDGE,"E37"),sQuery(id+"F16.wireOp",EDGE,"E38"),sQuery(id+"F16.wireOp",EDGE,"E39"),sQuery(id+"F16.wireOp",EDGE,"E40")])],"isStart":true}),makeQuery(id+"F18.opExtrude","CAP_FACE",FACE,{"disambiguationData":[OSD([subQ0,sQuery(id+"F17.wireOp",EDGE,"E42"),sQuery(id+"F17.wireOp",EDGE,"E43"),sQuery(id+"F17.wireOp",EDGE,"E44")])],"isStart":true}),makeQuery(id+"F18.opExtrude","CAP_FACE",FACE,{"disambiguationData":[OSD([sQuery(id+"F5.wireOp",EDGE,"E11.0")])],"isStart":true}),makeQuery(id+"F18.opExtrude","CAP_FACE",FACE,{"disambiguationData":[OSD([sQuery(id+"F5.wireOp",EDGE,"E12.0")])],"isStart":true})]})]}),makeQuery(id+"F23.opFillet","BLEND_FACE",FACE,{"disambiguationData":[OSD([subQ1,subQ0]),TDD([subQ2])]})],"blendedInto":[makeQuery(id+"F23.opFillet","BLEND_FACE",FACE,{"disambiguationData":[OSD([subQ1,subQ0]),TDD([subQ2])]})]});}
            var Q10;
            {var subQ2=sQuery(id+"F5.wireOp",EDGE,"E10.0");var subQ7=sQuery(id+"F17.wireOp",EDGE,"E41");var subQ21=makeQuery(id+"F18.opExtrude","SWEPT_FACE",FACE,{"disambiguationData":[OSD([subQ2])]});var subQ29=makeQuery(id+"F18.opExtrude","SWEPT_FACE",FACE,{"disambiguationData":[OSD([subQ7])]});Q10=makeQuery(id+"F28.opChamfer","BLEND_EDGE",EDGE,{"blendedFrom":[makeQuery(id+"F21.opBoolean","SPLIT",EDGE,{"disambiguationData":[TD([subQ21])],"derivedFrom":makeQuery(id+"F18.opExtrude","CAP_EDGE",EDGE,{"disambiguationData":[OSD([subQ7])],"isStart":true})}),makeQuery(id+"F21.opBoolean","SPLIT",FACE,{"disambiguationData":[TD([subQ21])],"derivedFrom":subQ29})],"blendedInto":[makeQuery(id+"F21.opBoolean","SPLIT",FACE,{"disambiguationData":[TD([subQ21])],"derivedFrom":subQ29})]});}
            var Q11;
            {var subQ0=sQuery(id+"F5.wireOp",EDGE,"E10.0");Q11=makeQuery(id+"F28.opChamfer","BLEND_EDGE",EDGE,{"blendedFrom":[makeQuery(id+"F18.opExtrude","CAP_EDGE",EDGE,{"disambiguationData":[OSD([subQ0])],"isStart":true}),makeQuery(id+"F18.opExtrude","SWEPT_FACE",FACE,{"disambiguationData":[OSD([subQ0])]})],"blendedInto":[makeQuery(id+"F18.opExtrude","SWEPT_FACE",FACE,{"disambiguationData":[OSD([subQ0])]})]});}
            var Q12;
            {var subQ0=sQuery(id+"F5.wireOp",EDGE,"E11.0");var subQ2=makeQuery(id+"F18.opExtrude","SWEPT_FACE",FACE,{"disambiguationData":[OSD([subQ0])]});var subQ17=sQuery(id+"F16.wireOp",EDGE,"E37");var subQ29=makeQuery(id+"F18.opExtrude","SWEPT_FACE",FACE,{"disambiguationData":[OSD([subQ17])]});Q12=makeQuery(id+"F27.opChamfer","BLEND_EDGE",EDGE,{"blendedFrom":[makeQuery(id+"F21.opBoolean","SPLIT",EDGE,{"disambiguationData":[TD([subQ2])],"derivedFrom":makeQuery(id+"F18.opExtrude","CAP_EDGE",EDGE,{"disambiguationData":[OSD([subQ17])],"isStart":false})}),makeQuery(id+"F21.opBoolean","SPLIT",FACE,{"disambiguationData":[TD([subQ2])],"derivedFrom":subQ29})],"blendedInto":[makeQuery(id+"F21.opBoolean","SPLIT",FACE,{"disambiguationData":[TD([subQ2])],"derivedFrom":subQ29})]});}
            var Q13;
            {var subQ0=sQuery(id+"F5.wireOp",EDGE,"E11.0");var subQ2=makeQuery(id+"F18.opExtrude","SWEPT_FACE",FACE,{"disambiguationData":[OSD([subQ0])]});var subQ17=sQuery(id+"F16.wireOp",EDGE,"E37");var subQ29=makeQuery(id+"F18.opExtrude","SWEPT_FACE",FACE,{"disambiguationData":[OSD([subQ17])]});Q13=makeQuery(id+"F28.opChamfer","BLEND_EDGE",EDGE,{"blendedFrom":[makeQuery(id+"F21.opBoolean","SPLIT",EDGE,{"disambiguationData":[TD([subQ2])],"derivedFrom":makeQuery(id+"F18.opExtrude","CAP_EDGE",EDGE,{"disambiguationData":[OSD([subQ17])],"isStart":true})}),makeQuery(id+"F21.opBoolean","SPLIT",FACE,{"disambiguationData":[TD([subQ2])],"derivedFrom":subQ29})],"blendedInto":[makeQuery(id+"F21.opBoolean","SPLIT",FACE,{"disambiguationData":[TD([subQ2])],"derivedFrom":subQ29})]});}
            var Q14;
            {var subQ0=sQuery(id+"F16.wireOp",EDGE,"E37");var subQ1=sQuery(id+"F1.wireOp",EDGE,"E1.0");var subQ2=makeQuery(id+"F21.opBoolean","INTERSECT",EDGE,{"disambiguationData":[OD(0.0)],"derivedFrom":[makeQuery(id+"F18.opExtrude","SWEPT_FACE",FACE,{"disambiguationData":[OSD([subQ1])]}),makeQuery(id+"F18.opExtrude","SWEPT_FACE",FACE,{"disambiguationData":[OSD([subQ0])]})]});Q14=makeQuery(id+"F28.opChamfer","BLEND_EDGE",EDGE,{"blendedFrom":[makeQuery(id+"F22.opFillet","BLEND_EDGE",EDGE,{"blendedFrom":[subQ2,makeQuery(id+"F21.opBoolean","MERGE",FACE,{"derivedFrom":[makeQuery(id+"F18.opExtrude","CAP_FACE",FACE,{"disambiguationData":[OSD([sQuery(id+"F0.wireOp",EDGE,"E0"),subQ1])],"isStart":true}),makeQuery(id+"F18.opExtrude","CAP_FACE",FACE,{"disambiguationData":[OSD([sQuery(id+"F4.wireOp",EDGE,"E9"),sQuery(id+"F5.wireOp",EDGE,"E10.0")])],"isStart":true}),makeQuery(id+"F18.opExtrude","CAP_FACE",FACE,{"disambiguationData":[OSD([sQuery(id+"F15.wireOp",EDGE,"E31"),sQuery(id+"F15.wireOp",EDGE,"E32"),sQuery(id+"F15.wireOp",EDGE,"E33"),sQuery(id+"F15.wireOp",EDGE,"E34"),sQuery(id+"F15.wireOp",EDGE,"E35"),sQuery(id+"F15.wireOp",EDGE,"E36")])],"isStart":true}),makeQuery(id+"F18.opExtrude","CAP_FACE",FACE,{"disambiguationData":[OSD([subQ0,sQuery(id+"F16.wireOp",EDGE,"E38"),sQuery(id+"F16.wireOp",EDGE,"E39"),sQuery(id+"F16.wireOp",EDGE,"E40")])],"isStart":true}),makeQuery(id+"F18.opExtrude","CAP_FACE",FACE,{"disambiguationData":[OSD([sQuery(id+"F17.wireOp",EDGE,"E41"),sQuery(id+"F17.wireOp",EDGE,"E42"),sQuery(id+"F17.wireOp",EDGE,"E43"),sQuery(id+"F17.wireOp",EDGE,"E44")])],"isStart":true}),makeQuery(id+"F18.opExtrude","CAP_FACE",FACE,{"disambiguationData":[OSD([sQuery(id+"F5.wireOp",EDGE,"E11.0")])],"isStart":true}),makeQuery(id+"F18.opExtrude","CAP_FACE",FACE,{"disambiguationData":[OSD([sQuery(id+"F5.wireOp",EDGE,"E12.0")])],"isStart":true})]})],"blendedInto":[makeQuery(id+"F21.opBoolean","MERGE",FACE,{"derivedFrom":[makeQuery(id+"F18.opExtrude","CAP_FACE",FACE,{"disambiguationData":[OSD([sQuery(id+"F0.wireOp",EDGE,"E0"),subQ1])],"isStart":true}),makeQuery(id+"F18.opExtrude","CAP_FACE",FACE,{"disambiguationData":[OSD([sQuery(id+"F4.wireOp",EDGE,"E9"),sQuery(id+"F5.wireOp",EDGE,"E10.0")])],"isStart":true}),makeQuery(id+"F18.opExtrude","CAP_FACE",FACE,{"disambiguationData":[OSD([sQuery(id+"F15.wireOp",EDGE,"E31"),sQuery(id+"F15.wireOp",EDGE,"E32"),sQuery(id+"F15.wireOp",EDGE,"E33"),sQuery(id+"F15.wireOp",EDGE,"E34"),sQuery(id+"F15.wireOp",EDGE,"E35"),sQuery(id+"F15.wireOp",EDGE,"E36")])],"isStart":true}),makeQuery(id+"F18.opExtrude","CAP_FACE",FACE,{"disambiguationData":[OSD([subQ0,sQuery(id+"F16.wireOp",EDGE,"E38"),sQuery(id+"F16.wireOp",EDGE,"E39"),sQuery(id+"F16.wireOp",EDGE,"E40")])],"isStart":true}),makeQuery(id+"F18.opExtrude","CAP_FACE",FACE,{"disambiguationData":[OSD([sQuery(id+"F17.wireOp",EDGE,"E41"),sQuery(id+"F17.wireOp",EDGE,"E42"),sQuery(id+"F17.wireOp",EDGE,"E43"),sQuery(id+"F17.wireOp",EDGE,"E44")])],"isStart":true}),makeQuery(id+"F18.opExtrude","CAP_FACE",FACE,{"disambiguationData":[OSD([sQuery(id+"F5.wireOp",EDGE,"E11.0")])],"isStart":true}),makeQuery(id+"F18.opExtrude","CAP_FACE",FACE,{"disambiguationData":[OSD([sQuery(id+"F5.wireOp",EDGE,"E12.0")])],"isStart":true})]})]}),makeQuery(id+"F22.opFillet","BLEND_FACE",FACE,{"disambiguationData":[OSD([subQ1,subQ0]),TDD([subQ2])]})],"blendedInto":[makeQuery(id+"F22.opFillet","BLEND_FACE",FACE,{"disambiguationData":[OSD([subQ1,subQ0]),TDD([subQ2])]})]});}
            var Q15;
            {var subQ0=sQuery(id+"F16.wireOp",EDGE,"E37");var subQ1=sQuery(id+"F1.wireOp",EDGE,"E1.0");var subQ2=makeQuery(id+"F21.opBoolean","INTERSECT",EDGE,{"disambiguationData":[OD(1.0)],"derivedFrom":[makeQuery(id+"F18.opExtrude","SWEPT_FACE",FACE,{"disambiguationData":[OSD([subQ1])]}),makeQuery(id+"F18.opExtrude","SWEPT_FACE",FACE,{"disambiguationData":[OSD([subQ0])]})]});Q15=makeQuery(id+"F28.opChamfer","BLEND_EDGE",EDGE,{"blendedFrom":[makeQuery(id+"F22.opFillet","BLEND_EDGE",EDGE,{"blendedFrom":[subQ2,makeQuery(id+"F21.opBoolean","MERGE",FACE,{"derivedFrom":[makeQuery(id+"F18.opExtrude","CAP_FACE",FACE,{"disambiguationData":[OSD([sQuery(id+"F0.wireOp",EDGE,"E0"),subQ1])],"isStart":true}),makeQuery(id+"F18.opExtrude","CAP_FACE",FACE,{"disambiguationData":[OSD([sQuery(id+"F4.wireOp",EDGE,"E9"),sQuery(id+"F5.wireOp",EDGE,"E10.0")])],"isStart":true}),makeQuery(id+"F18.opExtrude","CAP_FACE",FACE,{"disambiguationData":[OSD([sQuery(id+"F15.wireOp",EDGE,"E31"),sQuery(id+"F15.wireOp",EDGE,"E32"),sQuery(id+"F15.wireOp",EDGE,"E33"),sQuery(id+"F15.wireOp",EDGE,"E34"),sQuery(id+"F15.wireOp",EDGE,"E35"),sQuery(id+"F15.wireOp",EDGE,"E36")])],"isStart":true}),makeQuery(id+"F18.opExtrude","CAP_FACE",FACE,{"disambiguationData":[OSD([subQ0,sQuery(id+"F16.wireOp",EDGE,"E38"),sQuery(id+"F16.wireOp",EDGE,"E39"),sQuery(id+"F16.wireOp",EDGE,"E40")])],"isStart":true}),makeQuery(id+"F18.opExtrude","CAP_FACE",FACE,{"disambiguationData":[OSD([sQuery(id+"F17.wireOp",EDGE,"E41"),sQuery(id+"F17.wireOp",EDGE,"E42"),sQuery(id+"F17.wireOp",EDGE,"E43"),sQuery(id+"F17.wireOp",EDGE,"E44")])],"isStart":true}),makeQuery(id+"F18.opExtrude","CAP_FACE",FACE,{"disambiguationData":[OSD([sQuery(id+"F5.wireOp",EDGE,"E11.0")])],"isStart":true}),makeQuery(id+"F18.opExtrude","CAP_FACE",FACE,{"disambiguationData":[OSD([sQuery(id+"F5.wireOp",EDGE,"E12.0")])],"isStart":true})]})],"blendedInto":[makeQuery(id+"F21.opBoolean","MERGE",FACE,{"derivedFrom":[makeQuery(id+"F18.opExtrude","CAP_FACE",FACE,{"disambiguationData":[OSD([sQuery(id+"F0.wireOp",EDGE,"E0"),subQ1])],"isStart":true}),makeQuery(id+"F18.opExtrude","CAP_FACE",FACE,{"disambiguationData":[OSD([sQuery(id+"F4.wireOp",EDGE,"E9"),sQuery(id+"F5.wireOp",EDGE,"E10.0")])],"isStart":true}),makeQuery(id+"F18.opExtrude","CAP_FACE",FACE,{"disambiguationData":[OSD([sQuery(id+"F15.wireOp",EDGE,"E31"),sQuery(id+"F15.wireOp",EDGE,"E32"),sQuery(id+"F15.wireOp",EDGE,"E33"),sQuery(id+"F15.wireOp",EDGE,"E34"),sQuery(id+"F15.wireOp",EDGE,"E35"),sQuery(id+"F15.wireOp",EDGE,"E36")])],"isStart":true}),makeQuery(id+"F18.opExtrude","CAP_FACE",FACE,{"disambiguationData":[OSD([subQ0,sQuery(id+"F16.wireOp",EDGE,"E38"),sQuery(id+"F16.wireOp",EDGE,"E39"),sQuery(id+"F16.wireOp",EDGE,"E40")])],"isStart":true}),makeQuery(id+"F18.opExtrude","CAP_FACE",FACE,{"disambiguationData":[OSD([sQuery(id+"F17.wireOp",EDGE,"E41"),sQuery(id+"F17.wireOp",EDGE,"E42"),sQuery(id+"F17.wireOp",EDGE,"E43"),sQuery(id+"F17.wireOp",EDGE,"E44")])],"isStart":true}),makeQuery(id+"F18.opExtrude","CAP_FACE",FACE,{"disambiguationData":[OSD([sQuery(id+"F5.wireOp",EDGE,"E11.0")])],"isStart":true}),makeQuery(id+"F18.opExtrude","CAP_FACE",FACE,{"disambiguationData":[OSD([sQuery(id+"F5.wireOp",EDGE,"E12.0")])],"isStart":true})]})]}),makeQuery(id+"F22.opFillet","BLEND_FACE",FACE,{"disambiguationData":[OSD([subQ1,subQ0]),TDD([subQ2])]})],"blendedInto":[makeQuery(id+"F22.opFillet","BLEND_FACE",FACE,{"disambiguationData":[OSD([subQ1,subQ0]),TDD([subQ2])]})]});}
            var Q16;
            {var subQ0=sQuery(id+"F5.wireOp",EDGE,"E12.0");var subQ1=makeQuery(id+"F18.opExtrude","SWEPT_FACE",FACE,{"disambiguationData":[OSD([subQ0])]});var subQ17=sQuery(id+"F16.wireOp",EDGE,"E37");var subQ29=makeQuery(id+"F18.opExtrude","SWEPT_FACE",FACE,{"disambiguationData":[OSD([subQ17])]});Q16=makeQuery(id+"F28.opChamfer","BLEND_EDGE",EDGE,{"blendedFrom":[makeQuery(id+"F21.opBoolean","SPLIT",EDGE,{"disambiguationData":[TD([subQ1])],"derivedFrom":makeQuery(id+"F18.opExtrude","CAP_EDGE",EDGE,{"disambiguationData":[OSD([subQ17])],"isStart":true})}),makeQuery(id+"F21.opBoolean","SPLIT",FACE,{"disambiguationData":[TD([subQ1])],"derivedFrom":subQ29})],"blendedInto":[makeQuery(id+"F21.opBoolean","SPLIT",FACE,{"disambiguationData":[TD([subQ1])],"derivedFrom":subQ29})]});}
            var Q17;
            {var subQ0=sQuery(id+"F5.wireOp",EDGE,"E12.0");var subQ1=makeQuery(id+"F18.opExtrude","SWEPT_FACE",FACE,{"disambiguationData":[OSD([subQ0])]});var subQ16=sQuery(id+"F16.wireOp",EDGE,"E37");var subQ29=makeQuery(id+"F18.opExtrude","SWEPT_FACE",FACE,{"disambiguationData":[OSD([subQ16])]});Q17=makeQuery(id+"F27.opChamfer","BLEND_EDGE",EDGE,{"blendedFrom":[makeQuery(id+"F21.opBoolean","SPLIT",EDGE,{"disambiguationData":[TD([subQ1])],"derivedFrom":makeQuery(id+"F18.opExtrude","CAP_EDGE",EDGE,{"disambiguationData":[OSD([subQ16])],"isStart":false})}),makeQuery(id+"F21.opBoolean","SPLIT",FACE,{"disambiguationData":[TD([subQ1])],"derivedFrom":subQ29})],"blendedInto":[makeQuery(id+"F21.opBoolean","SPLIT",FACE,{"disambiguationData":[TD([subQ1])],"derivedFrom":subQ29})]});}
            var Q18;
            {var subQ0=sQuery(id+"F16.wireOp",EDGE,"E37");var subQ1=sQuery(id+"F1.wireOp",EDGE,"E1.0");var subQ2=makeQuery(id+"F21.opBoolean","INTERSECT",EDGE,{"disambiguationData":[OD(1.0)],"derivedFrom":[makeQuery(id+"F18.opExtrude","SWEPT_FACE",FACE,{"disambiguationData":[OSD([subQ1])]}),makeQuery(id+"F18.opExtrude","SWEPT_FACE",FACE,{"disambiguationData":[OSD([subQ0])]})]});Q18=makeQuery(id+"F27.opChamfer","BLEND_EDGE",EDGE,{"blendedFrom":[makeQuery(id+"F22.opFillet","BLEND_EDGE",EDGE,{"blendedFrom":[subQ2,makeQuery(id+"F21.opBoolean","MERGE",FACE,{"derivedFrom":[makeQuery(id+"F18.opExtrude","CAP_FACE",FACE,{"disambiguationData":[OSD([sQuery(id+"F0.wireOp",EDGE,"E0"),subQ1])],"isStart":false}),makeQuery(id+"F18.opExtrude","CAP_FACE",FACE,{"disambiguationData":[OSD([sQuery(id+"F4.wireOp",EDGE,"E9"),sQuery(id+"F5.wireOp",EDGE,"E10.0")])],"isStart":false}),makeQuery(id+"F18.opExtrude","CAP_FACE",FACE,{"disambiguationData":[OSD([sQuery(id+"F15.wireOp",EDGE,"E31"),sQuery(id+"F15.wireOp",EDGE,"E32"),sQuery(id+"F15.wireOp",EDGE,"E33"),sQuery(id+"F15.wireOp",EDGE,"E34"),sQuery(id+"F15.wireOp",EDGE,"E35"),sQuery(id+"F15.wireOp",EDGE,"E36")])],"isStart":false}),makeQuery(id+"F18.opExtrude","CAP_FACE",FACE,{"disambiguationData":[OSD([subQ0,sQuery(id+"F16.wireOp",EDGE,"E38"),sQuery(id+"F16.wireOp",EDGE,"E39"),sQuery(id+"F16.wireOp",EDGE,"E40")])],"isStart":false}),makeQuery(id+"F18.opExtrude","CAP_FACE",FACE,{"disambiguationData":[OSD([sQuery(id+"F17.wireOp",EDGE,"E41"),sQuery(id+"F17.wireOp",EDGE,"E42"),sQuery(id+"F17.wireOp",EDGE,"E43"),sQuery(id+"F17.wireOp",EDGE,"E44")])],"isStart":false}),makeQuery(id+"F18.opExtrude","CAP_FACE",FACE,{"disambiguationData":[OSD([sQuery(id+"F5.wireOp",EDGE,"E11.0")])],"isStart":false}),makeQuery(id+"F18.opExtrude","CAP_FACE",FACE,{"disambiguationData":[OSD([sQuery(id+"F5.wireOp",EDGE,"E12.0")])],"isStart":false})]})],"blendedInto":[makeQuery(id+"F21.opBoolean","MERGE",FACE,{"derivedFrom":[makeQuery(id+"F18.opExtrude","CAP_FACE",FACE,{"disambiguationData":[OSD([sQuery(id+"F0.wireOp",EDGE,"E0"),subQ1])],"isStart":false}),makeQuery(id+"F18.opExtrude","CAP_FACE",FACE,{"disambiguationData":[OSD([sQuery(id+"F4.wireOp",EDGE,"E9"),sQuery(id+"F5.wireOp",EDGE,"E10.0")])],"isStart":false}),makeQuery(id+"F18.opExtrude","CAP_FACE",FACE,{"disambiguationData":[OSD([sQuery(id+"F15.wireOp",EDGE,"E31"),sQuery(id+"F15.wireOp",EDGE,"E32"),sQuery(id+"F15.wireOp",EDGE,"E33"),sQuery(id+"F15.wireOp",EDGE,"E34"),sQuery(id+"F15.wireOp",EDGE,"E35"),sQuery(id+"F15.wireOp",EDGE,"E36")])],"isStart":false}),makeQuery(id+"F18.opExtrude","CAP_FACE",FACE,{"disambiguationData":[OSD([subQ0,sQuery(id+"F16.wireOp",EDGE,"E38"),sQuery(id+"F16.wireOp",EDGE,"E39"),sQuery(id+"F16.wireOp",EDGE,"E40")])],"isStart":false}),makeQuery(id+"F18.opExtrude","CAP_FACE",FACE,{"disambiguationData":[OSD([sQuery(id+"F17.wireOp",EDGE,"E41"),sQuery(id+"F17.wireOp",EDGE,"E42"),sQuery(id+"F17.wireOp",EDGE,"E43"),sQuery(id+"F17.wireOp",EDGE,"E44")])],"isStart":false}),makeQuery(id+"F18.opExtrude","CAP_FACE",FACE,{"disambiguationData":[OSD([sQuery(id+"F5.wireOp",EDGE,"E11.0")])],"isStart":false}),makeQuery(id+"F18.opExtrude","CAP_FACE",FACE,{"disambiguationData":[OSD([sQuery(id+"F5.wireOp",EDGE,"E12.0")])],"isStart":false})]})]}),makeQuery(id+"F22.opFillet","BLEND_FACE",FACE,{"disambiguationData":[OSD([subQ1,subQ0]),TDD([subQ2])]})],"blendedInto":[makeQuery(id+"F22.opFillet","BLEND_FACE",FACE,{"disambiguationData":[OSD([subQ1,subQ0]),TDD([subQ2])]})]});}
            var Q19;
            {var subQ0=sQuery(id+"F5.wireOp",EDGE,"E12.0");Q19=makeQuery(id+"F27.opChamfer","BLEND_EDGE",EDGE,{"blendedFrom":[makeQuery(id+"F18.opExtrude","CAP_EDGE",EDGE,{"disambiguationData":[OSD([subQ0])],"isStart":false}),makeQuery(id+"F18.opExtrude","SWEPT_FACE",FACE,{"disambiguationData":[OSD([subQ0])]})],"blendedInto":[makeQuery(id+"F18.opExtrude","SWEPT_FACE",FACE,{"disambiguationData":[OSD([subQ0])]})]});}
            var Q20;
            {var subQ0=sQuery(id+"F5.wireOp",EDGE,"E12.0");Q20=makeQuery(id+"F28.opChamfer","BLEND_EDGE",EDGE,{"blendedFrom":[makeQuery(id+"F18.opExtrude","CAP_EDGE",EDGE,{"disambiguationData":[OSD([subQ0])],"isStart":true}),makeQuery(id+"F18.opExtrude","SWEPT_FACE",FACE,{"disambiguationData":[OSD([subQ0])]})],"blendedInto":[makeQuery(id+"F18.opExtrude","SWEPT_FACE",FACE,{"disambiguationData":[OSD([subQ0])]})]});}
            var Q21;
            {var subQ0=sQuery(id+"F16.wireOp",EDGE,"E37");var subQ1=sQuery(id+"F1.wireOp",EDGE,"E1.0");var subQ2=makeQuery(id+"F21.opBoolean","INTERSECT",EDGE,{"disambiguationData":[OD(0.0)],"derivedFrom":[makeQuery(id+"F18.opExtrude","SWEPT_FACE",FACE,{"disambiguationData":[OSD([subQ1])]}),makeQuery(id+"F18.opExtrude","SWEPT_FACE",FACE,{"disambiguationData":[OSD([subQ0])]})]});Q21=makeQuery(id+"F27.opChamfer","BLEND_EDGE",EDGE,{"blendedFrom":[makeQuery(id+"F22.opFillet","BLEND_EDGE",EDGE,{"blendedFrom":[subQ2,makeQuery(id+"F21.opBoolean","MERGE",FACE,{"derivedFrom":[makeQuery(id+"F18.opExtrude","CAP_FACE",FACE,{"disambiguationData":[OSD([sQuery(id+"F0.wireOp",EDGE,"E0"),subQ1])],"isStart":false}),makeQuery(id+"F18.opExtrude","CAP_FACE",FACE,{"disambiguationData":[OSD([sQuery(id+"F4.wireOp",EDGE,"E9"),sQuery(id+"F5.wireOp",EDGE,"E10.0")])],"isStart":false}),makeQuery(id+"F18.opExtrude","CAP_FACE",FACE,{"disambiguationData":[OSD([sQuery(id+"F15.wireOp",EDGE,"E31"),sQuery(id+"F15.wireOp",EDGE,"E32"),sQuery(id+"F15.wireOp",EDGE,"E33"),sQuery(id+"F15.wireOp",EDGE,"E34"),sQuery(id+"F15.wireOp",EDGE,"E35"),sQuery(id+"F15.wireOp",EDGE,"E36")])],"isStart":false}),makeQuery(id+"F18.opExtrude","CAP_FACE",FACE,{"disambiguationData":[OSD([subQ0,sQuery(id+"F16.wireOp",EDGE,"E38"),sQuery(id+"F16.wireOp",EDGE,"E39"),sQuery(id+"F16.wireOp",EDGE,"E40")])],"isStart":false}),makeQuery(id+"F18.opExtrude","CAP_FACE",FACE,{"disambiguationData":[OSD([sQuery(id+"F17.wireOp",EDGE,"E41"),sQuery(id+"F17.wireOp",EDGE,"E42"),sQuery(id+"F17.wireOp",EDGE,"E43"),sQuery(id+"F17.wireOp",EDGE,"E44")])],"isStart":false}),makeQuery(id+"F18.opExtrude","CAP_FACE",FACE,{"disambiguationData":[OSD([sQuery(id+"F5.wireOp",EDGE,"E11.0")])],"isStart":false}),makeQuery(id+"F18.opExtrude","CAP_FACE",FACE,{"disambiguationData":[OSD([sQuery(id+"F5.wireOp",EDGE,"E12.0")])],"isStart":false})]})],"blendedInto":[makeQuery(id+"F21.opBoolean","MERGE",FACE,{"derivedFrom":[makeQuery(id+"F18.opExtrude","CAP_FACE",FACE,{"disambiguationData":[OSD([sQuery(id+"F0.wireOp",EDGE,"E0"),subQ1])],"isStart":false}),makeQuery(id+"F18.opExtrude","CAP_FACE",FACE,{"disambiguationData":[OSD([sQuery(id+"F4.wireOp",EDGE,"E9"),sQuery(id+"F5.wireOp",EDGE,"E10.0")])],"isStart":false}),makeQuery(id+"F18.opExtrude","CAP_FACE",FACE,{"disambiguationData":[OSD([sQuery(id+"F15.wireOp",EDGE,"E31"),sQuery(id+"F15.wireOp",EDGE,"E32"),sQuery(id+"F15.wireOp",EDGE,"E33"),sQuery(id+"F15.wireOp",EDGE,"E34"),sQuery(id+"F15.wireOp",EDGE,"E35"),sQuery(id+"F15.wireOp",EDGE,"E36")])],"isStart":false}),makeQuery(id+"F18.opExtrude","CAP_FACE",FACE,{"disambiguationData":[OSD([subQ0,sQuery(id+"F16.wireOp",EDGE,"E38"),sQuery(id+"F16.wireOp",EDGE,"E39"),sQuery(id+"F16.wireOp",EDGE,"E40")])],"isStart":false}),makeQuery(id+"F18.opExtrude","CAP_FACE",FACE,{"disambiguationData":[OSD([sQuery(id+"F17.wireOp",EDGE,"E41"),sQuery(id+"F17.wireOp",EDGE,"E42"),sQuery(id+"F17.wireOp",EDGE,"E43"),sQuery(id+"F17.wireOp",EDGE,"E44")])],"isStart":false}),makeQuery(id+"F18.opExtrude","CAP_FACE",FACE,{"disambiguationData":[OSD([sQuery(id+"F5.wireOp",EDGE,"E11.0")])],"isStart":false}),makeQuery(id+"F18.opExtrude","CAP_FACE",FACE,{"disambiguationData":[OSD([sQuery(id+"F5.wireOp",EDGE,"E12.0")])],"isStart":false})]})]}),makeQuery(id+"F22.opFillet","BLEND_FACE",FACE,{"disambiguationData":[OSD([subQ1,subQ0]),TDD([subQ2])]})],"blendedInto":[makeQuery(id+"F22.opFillet","BLEND_FACE",FACE,{"disambiguationData":[OSD([subQ1,subQ0]),TDD([subQ2])]})]});}
            var Q22;
            {var subQ0=sQuery(id+"F5.wireOp",EDGE,"E12.0");var subQ1=makeQuery(id+"F18.opExtrude","SWEPT_FACE",FACE,{"disambiguationData":[OSD([subQ0])]});var subQ26=sQuery(id+"F15.wireOp",EDGE,"E31");var subQ29=makeQuery(id+"F18.opExtrude","SWEPT_FACE",FACE,{"disambiguationData":[OSD([subQ26])]});Q22=makeQuery(id+"F27.opChamfer","BLEND_EDGE",EDGE,{"blendedFrom":[makeQuery(id+"F21.opBoolean","SPLIT",EDGE,{"disambiguationData":[TD([subQ1])],"derivedFrom":makeQuery(id+"F18.opExtrude","CAP_EDGE",EDGE,{"disambiguationData":[OSD([subQ26])],"isStart":false})}),makeQuery(id+"F21.opBoolean","SPLIT",FACE,{"disambiguationData":[TD([subQ1])],"derivedFrom":subQ29})],"blendedInto":[makeQuery(id+"F21.opBoolean","SPLIT",FACE,{"disambiguationData":[TD([subQ1])],"derivedFrom":subQ29})]});}
            var Q23;
            {var subQ0=sQuery(id+"F15.wireOp",EDGE,"E31");var subQ1=sQuery(id+"F1.wireOp",EDGE,"E1.0");var subQ2=makeQuery(id+"F21.opBoolean","INTERSECT",EDGE,{"disambiguationData":[OD(1.0)],"derivedFrom":[makeQuery(id+"F18.opExtrude","SWEPT_FACE",FACE,{"disambiguationData":[OSD([subQ1])]}),makeQuery(id+"F18.opExtrude","SWEPT_FACE",FACE,{"disambiguationData":[OSD([subQ0])]})]});Q23=makeQuery(id+"F27.opChamfer","BLEND_EDGE",EDGE,{"blendedFrom":[makeQuery(id+"F24.opFillet","BLEND_EDGE",EDGE,{"blendedFrom":[subQ2,makeQuery(id+"F21.opBoolean","MERGE",FACE,{"derivedFrom":[makeQuery(id+"F18.opExtrude","CAP_FACE",FACE,{"disambiguationData":[OSD([sQuery(id+"F0.wireOp",EDGE,"E0"),subQ1])],"isStart":false}),makeQuery(id+"F18.opExtrude","CAP_FACE",FACE,{"disambiguationData":[OSD([sQuery(id+"F4.wireOp",EDGE,"E9"),sQuery(id+"F5.wireOp",EDGE,"E10.0")])],"isStart":false}),makeQuery(id+"F18.opExtrude","CAP_FACE",FACE,{"disambiguationData":[OSD([subQ0,sQuery(id+"F15.wireOp",EDGE,"E32"),sQuery(id+"F15.wireOp",EDGE,"E33"),sQuery(id+"F15.wireOp",EDGE,"E34"),sQuery(id+"F15.wireOp",EDGE,"E35"),sQuery(id+"F15.wireOp",EDGE,"E36")])],"isStart":false}),makeQuery(id+"F18.opExtrude","CAP_FACE",FACE,{"disambiguationData":[OSD([sQuery(id+"F16.wireOp",EDGE,"E37"),sQuery(id+"F16.wireOp",EDGE,"E38"),sQuery(id+"F16.wireOp",EDGE,"E39"),sQuery(id+"F16.wireOp",EDGE,"E40")])],"isStart":false}),makeQuery(id+"F18.opExtrude","CAP_FACE",FACE,{"disambiguationData":[OSD([sQuery(id+"F17.wireOp",EDGE,"E41"),sQuery(id+"F17.wireOp",EDGE,"E42"),sQuery(id+"F17.wireOp",EDGE,"E43"),sQuery(id+"F17.wireOp",EDGE,"E44")])],"isStart":false}),makeQuery(id+"F18.opExtrude","CAP_FACE",FACE,{"disambiguationData":[OSD([sQuery(id+"F5.wireOp",EDGE,"E11.0")])],"isStart":false}),makeQuery(id+"F18.opExtrude","CAP_FACE",FACE,{"disambiguationData":[OSD([sQuery(id+"F5.wireOp",EDGE,"E12.0")])],"isStart":false})]})],"blendedInto":[makeQuery(id+"F21.opBoolean","MERGE",FACE,{"derivedFrom":[makeQuery(id+"F18.opExtrude","CAP_FACE",FACE,{"disambiguationData":[OSD([sQuery(id+"F0.wireOp",EDGE,"E0"),subQ1])],"isStart":false}),makeQuery(id+"F18.opExtrude","CAP_FACE",FACE,{"disambiguationData":[OSD([sQuery(id+"F4.wireOp",EDGE,"E9"),sQuery(id+"F5.wireOp",EDGE,"E10.0")])],"isStart":false}),makeQuery(id+"F18.opExtrude","CAP_FACE",FACE,{"disambiguationData":[OSD([subQ0,sQuery(id+"F15.wireOp",EDGE,"E32"),sQuery(id+"F15.wireOp",EDGE,"E33"),sQuery(id+"F15.wireOp",EDGE,"E34"),sQuery(id+"F15.wireOp",EDGE,"E35"),sQuery(id+"F15.wireOp",EDGE,"E36")])],"isStart":false}),makeQuery(id+"F18.opExtrude","CAP_FACE",FACE,{"disambiguationData":[OSD([sQuery(id+"F16.wireOp",EDGE,"E37"),sQuery(id+"F16.wireOp",EDGE,"E38"),sQuery(id+"F16.wireOp",EDGE,"E39"),sQuery(id+"F16.wireOp",EDGE,"E40")])],"isStart":false}),makeQuery(id+"F18.opExtrude","CAP_FACE",FACE,{"disambiguationData":[OSD([sQuery(id+"F17.wireOp",EDGE,"E41"),sQuery(id+"F17.wireOp",EDGE,"E42"),sQuery(id+"F17.wireOp",EDGE,"E43"),sQuery(id+"F17.wireOp",EDGE,"E44")])],"isStart":false}),makeQuery(id+"F18.opExtrude","CAP_FACE",FACE,{"disambiguationData":[OSD([sQuery(id+"F5.wireOp",EDGE,"E11.0")])],"isStart":false}),makeQuery(id+"F18.opExtrude","CAP_FACE",FACE,{"disambiguationData":[OSD([sQuery(id+"F5.wireOp",EDGE,"E12.0")])],"isStart":false})]})]}),makeQuery(id+"F24.opFillet","BLEND_FACE",FACE,{"disambiguationData":[OSD([subQ1,subQ0]),TDD([subQ2])]})],"blendedInto":[makeQuery(id+"F24.opFillet","BLEND_FACE",FACE,{"disambiguationData":[OSD([subQ1,subQ0]),TDD([subQ2])]})]});}
            var Q24;
            {var subQ0=sQuery(id+"F15.wireOp",EDGE,"E31");var subQ1=sQuery(id+"F1.wireOp",EDGE,"E1.0");var subQ2=makeQuery(id+"F21.opBoolean","INTERSECT",EDGE,{"disambiguationData":[OD(0.0)],"derivedFrom":[makeQuery(id+"F18.opExtrude","SWEPT_FACE",FACE,{"disambiguationData":[OSD([subQ1])]}),makeQuery(id+"F18.opExtrude","SWEPT_FACE",FACE,{"disambiguationData":[OSD([subQ0])]})]});Q24=makeQuery(id+"F27.opChamfer","BLEND_EDGE",EDGE,{"blendedFrom":[makeQuery(id+"F24.opFillet","BLEND_EDGE",EDGE,{"blendedFrom":[subQ2,makeQuery(id+"F21.opBoolean","MERGE",FACE,{"derivedFrom":[makeQuery(id+"F18.opExtrude","CAP_FACE",FACE,{"disambiguationData":[OSD([sQuery(id+"F0.wireOp",EDGE,"E0"),subQ1])],"isStart":false}),makeQuery(id+"F18.opExtrude","CAP_FACE",FACE,{"disambiguationData":[OSD([sQuery(id+"F4.wireOp",EDGE,"E9"),sQuery(id+"F5.wireOp",EDGE,"E10.0")])],"isStart":false}),makeQuery(id+"F18.opExtrude","CAP_FACE",FACE,{"disambiguationData":[OSD([subQ0,sQuery(id+"F15.wireOp",EDGE,"E32"),sQuery(id+"F15.wireOp",EDGE,"E33"),sQuery(id+"F15.wireOp",EDGE,"E34"),sQuery(id+"F15.wireOp",EDGE,"E35"),sQuery(id+"F15.wireOp",EDGE,"E36")])],"isStart":false}),makeQuery(id+"F18.opExtrude","CAP_FACE",FACE,{"disambiguationData":[OSD([sQuery(id+"F16.wireOp",EDGE,"E37"),sQuery(id+"F16.wireOp",EDGE,"E38"),sQuery(id+"F16.wireOp",EDGE,"E39"),sQuery(id+"F16.wireOp",EDGE,"E40")])],"isStart":false}),makeQuery(id+"F18.opExtrude","CAP_FACE",FACE,{"disambiguationData":[OSD([sQuery(id+"F17.wireOp",EDGE,"E41"),sQuery(id+"F17.wireOp",EDGE,"E42"),sQuery(id+"F17.wireOp",EDGE,"E43"),sQuery(id+"F17.wireOp",EDGE,"E44")])],"isStart":false}),makeQuery(id+"F18.opExtrude","CAP_FACE",FACE,{"disambiguationData":[OSD([sQuery(id+"F5.wireOp",EDGE,"E11.0")])],"isStart":false}),makeQuery(id+"F18.opExtrude","CAP_FACE",FACE,{"disambiguationData":[OSD([sQuery(id+"F5.wireOp",EDGE,"E12.0")])],"isStart":false})]})],"blendedInto":[makeQuery(id+"F21.opBoolean","MERGE",FACE,{"derivedFrom":[makeQuery(id+"F18.opExtrude","CAP_FACE",FACE,{"disambiguationData":[OSD([sQuery(id+"F0.wireOp",EDGE,"E0"),subQ1])],"isStart":false}),makeQuery(id+"F18.opExtrude","CAP_FACE",FACE,{"disambiguationData":[OSD([sQuery(id+"F4.wireOp",EDGE,"E9"),sQuery(id+"F5.wireOp",EDGE,"E10.0")])],"isStart":false}),makeQuery(id+"F18.opExtrude","CAP_FACE",FACE,{"disambiguationData":[OSD([subQ0,sQuery(id+"F15.wireOp",EDGE,"E32"),sQuery(id+"F15.wireOp",EDGE,"E33"),sQuery(id+"F15.wireOp",EDGE,"E34"),sQuery(id+"F15.wireOp",EDGE,"E35"),sQuery(id+"F15.wireOp",EDGE,"E36")])],"isStart":false}),makeQuery(id+"F18.opExtrude","CAP_FACE",FACE,{"disambiguationData":[OSD([sQuery(id+"F16.wireOp",EDGE,"E37"),sQuery(id+"F16.wireOp",EDGE,"E38"),sQuery(id+"F16.wireOp",EDGE,"E39"),sQuery(id+"F16.wireOp",EDGE,"E40")])],"isStart":false}),makeQuery(id+"F18.opExtrude","CAP_FACE",FACE,{"disambiguationData":[OSD([sQuery(id+"F17.wireOp",EDGE,"E41"),sQuery(id+"F17.wireOp",EDGE,"E42"),sQuery(id+"F17.wireOp",EDGE,"E43"),sQuery(id+"F17.wireOp",EDGE,"E44")])],"isStart":false}),makeQuery(id+"F18.opExtrude","CAP_FACE",FACE,{"disambiguationData":[OSD([sQuery(id+"F5.wireOp",EDGE,"E11.0")])],"isStart":false}),makeQuery(id+"F18.opExtrude","CAP_FACE",FACE,{"disambiguationData":[OSD([sQuery(id+"F5.wireOp",EDGE,"E12.0")])],"isStart":false})]})]}),makeQuery(id+"F24.opFillet","BLEND_FACE",FACE,{"disambiguationData":[OSD([subQ1,subQ0]),TDD([subQ2])]})],"blendedInto":[makeQuery(id+"F24.opFillet","BLEND_FACE",FACE,{"disambiguationData":[OSD([subQ1,subQ0]),TDD([subQ2])]})]});}
            var Q25;
            {var subQ2=sQuery(id+"F5.wireOp",EDGE,"E10.0");var subQ20=makeQuery(id+"F18.opExtrude","SWEPT_FACE",FACE,{"disambiguationData":[OSD([subQ2])]});var subQ26=sQuery(id+"F15.wireOp",EDGE,"E31");var subQ29=makeQuery(id+"F18.opExtrude","SWEPT_FACE",FACE,{"disambiguationData":[OSD([subQ26])]});Q25=makeQuery(id+"F27.opChamfer","BLEND_EDGE",EDGE,{"blendedFrom":[makeQuery(id+"F21.opBoolean","SPLIT",EDGE,{"disambiguationData":[TD([subQ20])],"derivedFrom":makeQuery(id+"F18.opExtrude","CAP_EDGE",EDGE,{"disambiguationData":[OSD([subQ26])],"isStart":false})}),makeQuery(id+"F21.opBoolean","SPLIT",FACE,{"disambiguationData":[TD([subQ20])],"derivedFrom":subQ29})],"blendedInto":[makeQuery(id+"F21.opBoolean","SPLIT",FACE,{"disambiguationData":[TD([subQ20])],"derivedFrom":subQ29})]});}
            var Q26;
            {var subQ2=sQuery(id+"F5.wireOp",EDGE,"E10.0");var subQ21=makeQuery(id+"F18.opExtrude","SWEPT_FACE",FACE,{"disambiguationData":[OSD([subQ2])]});var subQ27=sQuery(id+"F15.wireOp",EDGE,"E31");var subQ29=makeQuery(id+"F18.opExtrude","SWEPT_FACE",FACE,{"disambiguationData":[OSD([subQ27])]});Q26=makeQuery(id+"F28.opChamfer","BLEND_EDGE",EDGE,{"blendedFrom":[makeQuery(id+"F21.opBoolean","SPLIT",EDGE,{"disambiguationData":[TD([subQ21])],"derivedFrom":makeQuery(id+"F18.opExtrude","CAP_EDGE",EDGE,{"disambiguationData":[OSD([subQ27])],"isStart":true})}),makeQuery(id+"F21.opBoolean","SPLIT",FACE,{"disambiguationData":[TD([subQ21])],"derivedFrom":subQ29})],"blendedInto":[makeQuery(id+"F21.opBoolean","SPLIT",FACE,{"disambiguationData":[TD([subQ21])],"derivedFrom":subQ29})]});}
            var Q27;
            {var subQ0=sQuery(id+"F15.wireOp",EDGE,"E31");var subQ1=sQuery(id+"F1.wireOp",EDGE,"E1.0");var subQ2=makeQuery(id+"F21.opBoolean","INTERSECT",EDGE,{"disambiguationData":[OD(0.0)],"derivedFrom":[makeQuery(id+"F18.opExtrude","SWEPT_FACE",FACE,{"disambiguationData":[OSD([subQ1])]}),makeQuery(id+"F18.opExtrude","SWEPT_FACE",FACE,{"disambiguationData":[OSD([subQ0])]})]});Q27=makeQuery(id+"F28.opChamfer","BLEND_EDGE",EDGE,{"blendedFrom":[makeQuery(id+"F24.opFillet","BLEND_EDGE",EDGE,{"blendedFrom":[subQ2,makeQuery(id+"F21.opBoolean","MERGE",FACE,{"derivedFrom":[makeQuery(id+"F18.opExtrude","CAP_FACE",FACE,{"disambiguationData":[OSD([sQuery(id+"F0.wireOp",EDGE,"E0"),subQ1])],"isStart":true}),makeQuery(id+"F18.opExtrude","CAP_FACE",FACE,{"disambiguationData":[OSD([sQuery(id+"F4.wireOp",EDGE,"E9"),sQuery(id+"F5.wireOp",EDGE,"E10.0")])],"isStart":true}),makeQuery(id+"F18.opExtrude","CAP_FACE",FACE,{"disambiguationData":[OSD([subQ0,sQuery(id+"F15.wireOp",EDGE,"E32"),sQuery(id+"F15.wireOp",EDGE,"E33"),sQuery(id+"F15.wireOp",EDGE,"E34"),sQuery(id+"F15.wireOp",EDGE,"E35"),sQuery(id+"F15.wireOp",EDGE,"E36")])],"isStart":true}),makeQuery(id+"F18.opExtrude","CAP_FACE",FACE,{"disambiguationData":[OSD([sQuery(id+"F16.wireOp",EDGE,"E37"),sQuery(id+"F16.wireOp",EDGE,"E38"),sQuery(id+"F16.wireOp",EDGE,"E39"),sQuery(id+"F16.wireOp",EDGE,"E40")])],"isStart":true}),makeQuery(id+"F18.opExtrude","CAP_FACE",FACE,{"disambiguationData":[OSD([sQuery(id+"F17.wireOp",EDGE,"E41"),sQuery(id+"F17.wireOp",EDGE,"E42"),sQuery(id+"F17.wireOp",EDGE,"E43"),sQuery(id+"F17.wireOp",EDGE,"E44")])],"isStart":true}),makeQuery(id+"F18.opExtrude","CAP_FACE",FACE,{"disambiguationData":[OSD([sQuery(id+"F5.wireOp",EDGE,"E11.0")])],"isStart":true}),makeQuery(id+"F18.opExtrude","CAP_FACE",FACE,{"disambiguationData":[OSD([sQuery(id+"F5.wireOp",EDGE,"E12.0")])],"isStart":true})]})],"blendedInto":[makeQuery(id+"F21.opBoolean","MERGE",FACE,{"derivedFrom":[makeQuery(id+"F18.opExtrude","CAP_FACE",FACE,{"disambiguationData":[OSD([sQuery(id+"F0.wireOp",EDGE,"E0"),subQ1])],"isStart":true}),makeQuery(id+"F18.opExtrude","CAP_FACE",FACE,{"disambiguationData":[OSD([sQuery(id+"F4.wireOp",EDGE,"E9"),sQuery(id+"F5.wireOp",EDGE,"E10.0")])],"isStart":true}),makeQuery(id+"F18.opExtrude","CAP_FACE",FACE,{"disambiguationData":[OSD([subQ0,sQuery(id+"F15.wireOp",EDGE,"E32"),sQuery(id+"F15.wireOp",EDGE,"E33"),sQuery(id+"F15.wireOp",EDGE,"E34"),sQuery(id+"F15.wireOp",EDGE,"E35"),sQuery(id+"F15.wireOp",EDGE,"E36")])],"isStart":true}),makeQuery(id+"F18.opExtrude","CAP_FACE",FACE,{"disambiguationData":[OSD([sQuery(id+"F16.wireOp",EDGE,"E37"),sQuery(id+"F16.wireOp",EDGE,"E38"),sQuery(id+"F16.wireOp",EDGE,"E39"),sQuery(id+"F16.wireOp",EDGE,"E40")])],"isStart":true}),makeQuery(id+"F18.opExtrude","CAP_FACE",FACE,{"disambiguationData":[OSD([sQuery(id+"F17.wireOp",EDGE,"E41"),sQuery(id+"F17.wireOp",EDGE,"E42"),sQuery(id+"F17.wireOp",EDGE,"E43"),sQuery(id+"F17.wireOp",EDGE,"E44")])],"isStart":true}),makeQuery(id+"F18.opExtrude","CAP_FACE",FACE,{"disambiguationData":[OSD([sQuery(id+"F5.wireOp",EDGE,"E11.0")])],"isStart":true}),makeQuery(id+"F18.opExtrude","CAP_FACE",FACE,{"disambiguationData":[OSD([sQuery(id+"F5.wireOp",EDGE,"E12.0")])],"isStart":true})]})]}),makeQuery(id+"F24.opFillet","BLEND_FACE",FACE,{"disambiguationData":[OSD([subQ1,subQ0]),TDD([subQ2])]})],"blendedInto":[makeQuery(id+"F24.opFillet","BLEND_FACE",FACE,{"disambiguationData":[OSD([subQ1,subQ0]),TDD([subQ2])]})]});}
            var Q28;
            {var subQ0=sQuery(id+"F15.wireOp",EDGE,"E31");var subQ1=sQuery(id+"F1.wireOp",EDGE,"E1.0");var subQ2=makeQuery(id+"F21.opBoolean","INTERSECT",EDGE,{"disambiguationData":[OD(1.0)],"derivedFrom":[makeQuery(id+"F18.opExtrude","SWEPT_FACE",FACE,{"disambiguationData":[OSD([subQ1])]}),makeQuery(id+"F18.opExtrude","SWEPT_FACE",FACE,{"disambiguationData":[OSD([subQ0])]})]});Q28=makeQuery(id+"F28.opChamfer","BLEND_EDGE",EDGE,{"blendedFrom":[makeQuery(id+"F24.opFillet","BLEND_EDGE",EDGE,{"blendedFrom":[subQ2,makeQuery(id+"F21.opBoolean","MERGE",FACE,{"derivedFrom":[makeQuery(id+"F18.opExtrude","CAP_FACE",FACE,{"disambiguationData":[OSD([sQuery(id+"F0.wireOp",EDGE,"E0"),subQ1])],"isStart":true}),makeQuery(id+"F18.opExtrude","CAP_FACE",FACE,{"disambiguationData":[OSD([sQuery(id+"F4.wireOp",EDGE,"E9"),sQuery(id+"F5.wireOp",EDGE,"E10.0")])],"isStart":true}),makeQuery(id+"F18.opExtrude","CAP_FACE",FACE,{"disambiguationData":[OSD([subQ0,sQuery(id+"F15.wireOp",EDGE,"E32"),sQuery(id+"F15.wireOp",EDGE,"E33"),sQuery(id+"F15.wireOp",EDGE,"E34"),sQuery(id+"F15.wireOp",EDGE,"E35"),sQuery(id+"F15.wireOp",EDGE,"E36")])],"isStart":true}),makeQuery(id+"F18.opExtrude","CAP_FACE",FACE,{"disambiguationData":[OSD([sQuery(id+"F16.wireOp",EDGE,"E37"),sQuery(id+"F16.wireOp",EDGE,"E38"),sQuery(id+"F16.wireOp",EDGE,"E39"),sQuery(id+"F16.wireOp",EDGE,"E40")])],"isStart":true}),makeQuery(id+"F18.opExtrude","CAP_FACE",FACE,{"disambiguationData":[OSD([sQuery(id+"F17.wireOp",EDGE,"E41"),sQuery(id+"F17.wireOp",EDGE,"E42"),sQuery(id+"F17.wireOp",EDGE,"E43"),sQuery(id+"F17.wireOp",EDGE,"E44")])],"isStart":true}),makeQuery(id+"F18.opExtrude","CAP_FACE",FACE,{"disambiguationData":[OSD([sQuery(id+"F5.wireOp",EDGE,"E11.0")])],"isStart":true}),makeQuery(id+"F18.opExtrude","CAP_FACE",FACE,{"disambiguationData":[OSD([sQuery(id+"F5.wireOp",EDGE,"E12.0")])],"isStart":true})]})],"blendedInto":[makeQuery(id+"F21.opBoolean","MERGE",FACE,{"derivedFrom":[makeQuery(id+"F18.opExtrude","CAP_FACE",FACE,{"disambiguationData":[OSD([sQuery(id+"F0.wireOp",EDGE,"E0"),subQ1])],"isStart":true}),makeQuery(id+"F18.opExtrude","CAP_FACE",FACE,{"disambiguationData":[OSD([sQuery(id+"F4.wireOp",EDGE,"E9"),sQuery(id+"F5.wireOp",EDGE,"E10.0")])],"isStart":true}),makeQuery(id+"F18.opExtrude","CAP_FACE",FACE,{"disambiguationData":[OSD([subQ0,sQuery(id+"F15.wireOp",EDGE,"E32"),sQuery(id+"F15.wireOp",EDGE,"E33"),sQuery(id+"F15.wireOp",EDGE,"E34"),sQuery(id+"F15.wireOp",EDGE,"E35"),sQuery(id+"F15.wireOp",EDGE,"E36")])],"isStart":true}),makeQuery(id+"F18.opExtrude","CAP_FACE",FACE,{"disambiguationData":[OSD([sQuery(id+"F16.wireOp",EDGE,"E37"),sQuery(id+"F16.wireOp",EDGE,"E38"),sQuery(id+"F16.wireOp",EDGE,"E39"),sQuery(id+"F16.wireOp",EDGE,"E40")])],"isStart":true}),makeQuery(id+"F18.opExtrude","CAP_FACE",FACE,{"disambiguationData":[OSD([sQuery(id+"F17.wireOp",EDGE,"E41"),sQuery(id+"F17.wireOp",EDGE,"E42"),sQuery(id+"F17.wireOp",EDGE,"E43"),sQuery(id+"F17.wireOp",EDGE,"E44")])],"isStart":true}),makeQuery(id+"F18.opExtrude","CAP_FACE",FACE,{"disambiguationData":[OSD([sQuery(id+"F5.wireOp",EDGE,"E11.0")])],"isStart":true}),makeQuery(id+"F18.opExtrude","CAP_FACE",FACE,{"disambiguationData":[OSD([sQuery(id+"F5.wireOp",EDGE,"E12.0")])],"isStart":true})]})]}),makeQuery(id+"F24.opFillet","BLEND_FACE",FACE,{"disambiguationData":[OSD([subQ1,subQ0]),TDD([subQ2])]})],"blendedInto":[makeQuery(id+"F24.opFillet","BLEND_FACE",FACE,{"disambiguationData":[OSD([subQ1,subQ0]),TDD([subQ2])]})]});}
            var Q29;
            {var subQ0=sQuery(id+"F5.wireOp",EDGE,"E12.0");var subQ1=makeQuery(id+"F18.opExtrude","SWEPT_FACE",FACE,{"disambiguationData":[OSD([subQ0])]});var subQ27=sQuery(id+"F15.wireOp",EDGE,"E31");var subQ29=makeQuery(id+"F18.opExtrude","SWEPT_FACE",FACE,{"disambiguationData":[OSD([subQ27])]});Q29=makeQuery(id+"F28.opChamfer","BLEND_EDGE",EDGE,{"blendedFrom":[makeQuery(id+"F21.opBoolean","SPLIT",EDGE,{"disambiguationData":[TD([subQ1])],"derivedFrom":makeQuery(id+"F18.opExtrude","CAP_EDGE",EDGE,{"disambiguationData":[OSD([subQ27])],"isStart":true})}),makeQuery(id+"F21.opBoolean","SPLIT",FACE,{"disambiguationData":[TD([subQ1])],"derivedFrom":subQ29})],"blendedInto":[makeQuery(id+"F21.opBoolean","SPLIT",FACE,{"disambiguationData":[TD([subQ1])],"derivedFrom":subQ29})]});}
            fillet(context, id + "F29", {"entities" : qUnion([Q0, Q1, Q2, Q3, Q4, Q5, Q6, Q7, Q8, Q9, Q10, Q11, Q12, Q13, Q14, Q15, Q16, Q17, Q18, Q19, Q20, Q21, Q22, Q23, Q24, Q25, Q26, Q27, Q28, Q29]), "radius" : 2 * mm, "tangentPropagation" : true, "allowEdgeOverflow" : false});
        }
        {
            var Q0;
            Q0=makeQuery(id+"F19.boolean.opBoolean","COPY",EDGE,{"derivedFrom":makeQuery(id+"F19.opExtrude","CAP_EDGE",EDGE,{"disambiguationData":[OSD([sQuery(id+"F3.wireOp",EDGE,"E6")])],"isStart":true})});
            var Q1;
            Q1=makeQuery(id+"F18.opExtrude","CAP_EDGE",EDGE,{"disambiguationData":[OSD([sQuery(id+"F0.wireOp",EDGE,"E0")])],"isStart":true});
            var Q2;
            Q2=makeQuery(id+"F20.boolean.opBoolean","COPY",EDGE,{"derivedFrom":makeQuery(id+"F20.opExtrude","CAP_EDGE",EDGE,{"disambiguationData":[OSD([sQuery(id+"F2.wireOp",EDGE,"E2")])],"isStart":true})});
            var Q3;
            Q3=makeQuery(id+"F18.opExtrude","CAP_EDGE",EDGE,{"disambiguationData":[OSD([sQuery(id+"F4.wireOp",EDGE,"E9")])],"isStart":true});
            chamfer(context, id + "F30", {"entities" : qUnion([Q0, Q1, Q2, Q3]), "width" : 0.5 * mm, "tangentPropagation" : true});
        }
    });
